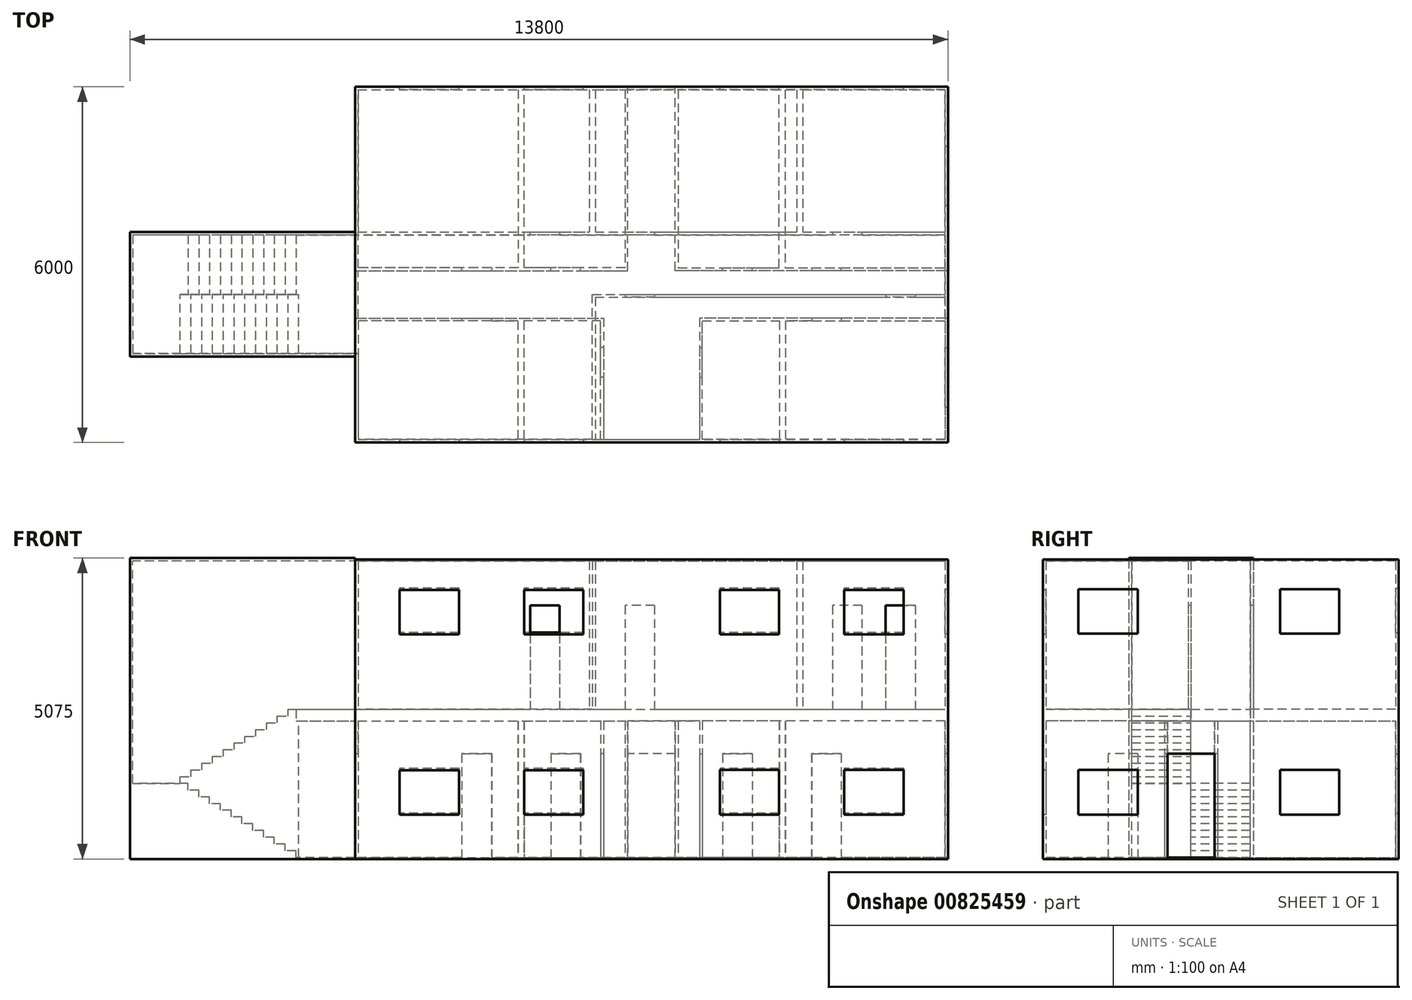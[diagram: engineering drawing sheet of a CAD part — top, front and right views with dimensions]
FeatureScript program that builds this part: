
annotation { "Feature Type Name" : "Feature", "Feature Type Description" : "" }
export const myFeature = defineFeature(function(context is Context, id is Id, definition is map)
    precondition{}
    {
        {
            var Q0;
            Q0=qCreatedBy(makeId("Top.planeOp"),FACE);
            var sketch = newSketch(context, id + "F0", { "sketchPlane" : qUnion([Q0])});
            skLineSegment(sketch, "E0.bottom", {"start": v(0, 0) * mm, "end": v(10000, 0) * mm});
            skLineSegment(sketch, "E0.top", {"start": v(0, 6000) * mm, "end": v(10000, 6000) * mm});
            skLineSegment(sketch, "E0.left", {"start": v(0, 0) * mm, "end": v(0, 6000) * mm});
            skLineSegment(sketch, "E0.right", {"start": v(10000, 0) * mm, "end": v(10000, 6000) * mm});
            skSolve(sketch);
        }
        {
            var Q0;
            Q0=qCreatedBy(makeId("Top.planeOp"),FACE);
            var sketch = newSketch(context, id + "F1", { "sketchPlane" : qUnion([Q0])});
            skLineSegment(sketch, "E1.bottom", {"start": v(0, 0) * mm, "end": v(5000, 0) * mm});
            skLineSegment(sketch, "E1.top", {"start": v(0, 6000) * mm, "end": v(4600, 6000) * mm});
            skLineSegment(sketch, "E1.left", {"start": v(0, 0) * mm, "end": v(0, 2100) * mm});
            skLineSegment(sketch, "E2", {"start": v(0, 2900) * mm, "end": v(1800, 2900) * mm});
            skLineSegment(sketch, "E3", {"start": v(0, 2100) * mm, "end": v(1800, 2100) * mm});
            skLineSegment(sketch, "E4", {"start": v(2800, 2900) * mm, "end": v(2800, 6000) * mm});
            skLineSegment(sketch, "E5", {"start": v(2792.35, 2100) * mm, "end": v(2792.35, 0) * mm});
            skLineSegment(sketch, "E6", {"start": v(2800, 2900) * mm, "end": v(3300, 2900) * mm});
            skLineSegment(sketch, "E7", {"start": v(4600, 2900) * mm, "end": v(4600, 6000) * mm});
            skLineSegment(sketch, "E8", {"start": v(2792.35, 2100) * mm, "end": v(4192.35, 2100) * mm});
            skLineSegment(sketch, "E9", {"start": v(4192.35, 2100) * mm, "end": v(4192.35, 1600) * mm});
            skPoint(sketch, "E10", {"position": v(1800, 2900) * mm});
            skPoint(sketch, "E11", {"position": v(2300, 2900) * mm});
            skPoint(sketch, "E12", {"position": v(1800, 2100) * mm});
            skPoint(sketch, "E13", {"position": v(2300, 2100) * mm});
            skPoint(sketch, "E14", {"position": v(4192.35, 1600) * mm});
            skPoint(sketch, "E15", {"position": v(3300, 2900) * mm});
            skPoint(sketch, "E16", {"position": v(3800, 2900) * mm});
            skPoint(sketch, "E17", {"position": v(4192.35, 1100) * mm});
            skLineSegment(sketch, "E18.trimOffspring", {"start": v(2300, 2900) * mm, "end": v(2800, 2900) * mm});
            skLineSegment(sketch, "E19.trimOffspring", {"start": v(2300, 2100) * mm, "end": v(2792.35, 2100) * mm});
            skLineSegment(sketch, "E20.trimOffspring", {"start": v(3800, 2900) * mm, "end": v(4600, 2900) * mm});
            skLineSegment(sketch, "E21.trimOffspring", {"start": v(4192.35, 1100) * mm, "end": v(4192.35, 0) * mm});
            skLineSegment(sketch, "E22.trimOffspring", {"start": v(0, 2900) * mm, "end": v(0, 6000) * mm});
            skLineSegment(sketch, "E23", {"start": v(1800, 2100) * mm, "end": v(1800, 2050) * mm});
            skLineSegment(sketch, "E24", {"start": v(1800, 2050) * mm, "end": v(50, 2050) * mm});
            skLineSegment(sketch, "E25", {"start": v(50, 2050) * mm, "end": v(50, 50) * mm});
            skLineSegment(sketch, "E26", {"start": v(50, 50) * mm, "end": v(2742.35, 50) * mm});
            skLineSegment(sketch, "E27", {"start": v(2300, 2100) * mm, "end": v(2300, 2050) * mm});
            skLineSegment(sketch, "E28", {"start": v(2300, 2050) * mm, "end": v(2742.35, 2050) * mm});
            skLineSegment(sketch, "E29", {"start": v(2742.35, 2050) * mm, "end": v(2742.35, 50) * mm});
            skLineSegment(sketch, "E30", {"start": v(4192.35, 1600) * mm, "end": v(4142.35, 1600) * mm});
            skLineSegment(sketch, "E31", {"start": v(4142.35, 1600) * mm, "end": v(4142.35, 2050) * mm});
            skLineSegment(sketch, "E32", {"start": v(4142.35, 2050) * mm, "end": v(2842.35, 2050) * mm});
            skLineSegment(sketch, "E33", {"start": v(2842.35, 2050) * mm, "end": v(2842.35, 50) * mm});
            skLineSegment(sketch, "E34", {"start": v(2842.35, 50) * mm, "end": v(4142.35, 50) * mm});
            skLineSegment(sketch, "E35", {"start": v(4192.35, 1100) * mm, "end": v(4142.35, 1100) * mm});
            skLineSegment(sketch, "E36", {"start": v(4142.35, 50) * mm, "end": v(4142.35, 1100) * mm});
            skLineSegment(sketch, "E37", {"start": v(4192.35, 50) * mm, "end": v(5000, 50) * mm});
            skLineSegment(sketch, "E38", {"start": v(5000, 0) * mm, "end": v(5000, 50) * mm});
            skLineSegment(sketch, "E39", {"start": v(1800, 2900) * mm, "end": v(1800, 2950) * mm});
            skLineSegment(sketch, "E40", {"start": v(1800, 2950) * mm, "end": v(50, 2950) * mm});
            skLineSegment(sketch, "E41", {"start": v(50, 2950) * mm, "end": v(50, 5950) * mm});
            skLineSegment(sketch, "E42", {"start": v(50, 5950) * mm, "end": v(2750, 5950) * mm});
            skLineSegment(sketch, "E43", {"start": v(2750, 5950) * mm, "end": v(2750, 2950) * mm});
            skLineSegment(sketch, "E44", {"start": v(2750, 2950) * mm, "end": v(2303.7, 2950) * mm});
            skLineSegment(sketch, "E45", {"start": v(2303.7, 2950) * mm, "end": v(2300, 2900) * mm});
            skLineSegment(sketch, "E46", {"start": v(3300, 2900) * mm, "end": v(3300, 2950) * mm});
            skLineSegment(sketch, "E47", {"start": v(3300, 2950) * mm, "end": v(2850, 2950) * mm});
            skLineSegment(sketch, "E48", {"start": v(2850, 2950) * mm, "end": v(2850, 5950) * mm});
            skLineSegment(sketch, "E49", {"start": v(2850, 5950) * mm, "end": v(4550, 5950) * mm});
            skLineSegment(sketch, "E50", {"start": v(4550, 5950) * mm, "end": v(4550, 2950) * mm});
            skLineSegment(sketch, "E51", {"start": v(4550, 2950) * mm, "end": v(3800.9, 2950) * mm});
            skLineSegment(sketch, "E52", {"start": v(3800, 2900) * mm, "end": v(3800.9, 2950) * mm});
            skSolve(sketch);
        }
        {
            var Q0;
            Q0=qSketchRegion(id+"F0",true);
            extrude(context, id + "F2", {"entities" : qUnion([Q0]), "oppositeDirection" : true, "depth" : 25 * mm, "offsetDistance" : 25 * mm});
        }
        {
            var Q0;
            Q0=qSketchRegion(id+"F1",true);
            extrude(context, id + "F3", {"entities" : qUnion([Q0]), "operationType" : NewBodyOperationType.ADD, "depth" : 2500 * mm, "offsetDistance" : 25 * mm});
        }
        {
            var Q0;
            Q0=qCreatedBy(makeId("Top.planeOp"),FACE);
            cPlane(context, id + "F4", {"entities" : qUnion([Q0]), "cplaneType" : CPlaneType.OFFSET, "offset" : 2500 * mm, "width" : 150 * mm, "height" : 150 * mm});
        }
        {
            var Q0;
            Q0=qCreatedBy(id+"F4.planeOp",FACE);
            var sketch = newSketch(context, id + "F5", { "sketchPlane" : qUnion([Q0])});
            skLineSegment(sketch, "E53.bottom", {"start": v(0, 0) * mm, "end": v(10000, 0) * mm});
            skLineSegment(sketch, "E53.top", {"start": v(0, 6000) * mm, "end": v(10000, 6000) * mm});
            skLineSegment(sketch, "E53.left", {"start": v(0, 0) * mm, "end": v(0, 6000) * mm});
            skLineSegment(sketch, "E53.right", {"start": v(10000, 0) * mm, "end": v(10000, 6000) * mm});
            skSolve(sketch);
        }
        {
            var Q0;
            Q0=qSketchRegion(id+"F5",true);
            extrude(context, id + "F6", {"entities" : qUnion([Q0]), "operationType" : NewBodyOperationType.ADD, "oppositeDirection" : true, "depth" : 200 * mm, "offsetDistance" : 25 * mm});
        }
        {
            var Q0;
            Q0=qCreatedBy(id+"F4.planeOp",FACE);
            var sketch = newSketch(context, id + "F7", { "sketchPlane" : qUnion([Q0])});
            skLineSegment(sketch, "E54.bottom", {"start": v(0, 0) * mm, "end": v(5000, 0) * mm});
            skLineSegment(sketch, "E54.top", {"start": v(0, 6000) * mm, "end": v(4600, 6000) * mm});
            skLineSegment(sketch, "E54.left", {"start": v(0, 0) * mm, "end": v(0, 2100) * mm});
            skLineSegment(sketch, "E55", {"start": v(0, 2900) * mm, "end": v(1800, 2900) * mm});
            skLineSegment(sketch, "E56", {"start": v(0, 2100) * mm, "end": v(1800, 2100) * mm});
            skLineSegment(sketch, "E57", {"start": v(2800, 2900) * mm, "end": v(2800, 6000) * mm});
            skLineSegment(sketch, "E58", {"start": v(2792.35, 2100) * mm, "end": v(2792.35, 0) * mm});
            skLineSegment(sketch, "E59", {"start": v(2800, 2900) * mm, "end": v(3300, 2900) * mm});
            skLineSegment(sketch, "E60", {"start": v(4600, 2900) * mm, "end": v(4600, 6000) * mm});
            skLineSegment(sketch, "E61", {"start": v(2792.35, 2100) * mm, "end": v(4192.35, 2100) * mm});
            skLineSegment(sketch, "E62", {"start": v(4192.35, 2100) * mm, "end": v(4192.35, 1600) * mm});
            skPoint(sketch, "E63", {"position": v(1800, 2900) * mm});
            skPoint(sketch, "E64", {"position": v(2300, 2900) * mm});
            skPoint(sketch, "E65", {"position": v(1800, 2100) * mm});
            skPoint(sketch, "E66", {"position": v(2300, 2100) * mm});
            skPoint(sketch, "E67", {"position": v(4192.35, 1600) * mm});
            skPoint(sketch, "E68", {"position": v(3300, 2900) * mm});
            skPoint(sketch, "E69", {"position": v(3800, 2900) * mm});
            skPoint(sketch, "E70", {"position": v(4192.35, 1100) * mm});
            skLineSegment(sketch, "E71.trimOffspring", {"start": v(2300, 2900) * mm, "end": v(2800, 2900) * mm});
            skLineSegment(sketch, "E72.trimOffspring", {"start": v(2300, 2100) * mm, "end": v(2792.35, 2100) * mm});
            skLineSegment(sketch, "E73.trimOffspring", {"start": v(3800, 2900) * mm, "end": v(4600, 2900) * mm});
            skLineSegment(sketch, "E74.trimOffspring", {"start": v(4192.35, 1100) * mm, "end": v(4192.35, 0) * mm});
            skLineSegment(sketch, "E75.trimOffspring", {"start": v(0, 2900) * mm, "end": v(0, 6000) * mm});
            skLineSegment(sketch, "E76", {"start": v(1800, 2100) * mm, "end": v(1800, 2050) * mm});
            skLineSegment(sketch, "E77", {"start": v(1800, 2050) * mm, "end": v(50, 2050) * mm});
            skLineSegment(sketch, "E78", {"start": v(50, 2050) * mm, "end": v(50, 50) * mm});
            skLineSegment(sketch, "E79", {"start": v(50, 50) * mm, "end": v(2742.35, 50) * mm});
            skLineSegment(sketch, "E80", {"start": v(2300, 2100) * mm, "end": v(2300, 2050) * mm});
            skLineSegment(sketch, "E81", {"start": v(2300, 2050) * mm, "end": v(2742.35, 2050) * mm});
            skLineSegment(sketch, "E82", {"start": v(2742.35, 2050) * mm, "end": v(2742.35, 50) * mm});
            skLineSegment(sketch, "E83", {"start": v(4192.35, 1600) * mm, "end": v(4142.35, 1600) * mm});
            skLineSegment(sketch, "E84", {"start": v(4142.35, 1600) * mm, "end": v(4142.35, 2050) * mm});
            skLineSegment(sketch, "E85", {"start": v(4142.35, 2050) * mm, "end": v(2842.35, 2050) * mm});
            skLineSegment(sketch, "E86", {"start": v(2842.35, 2050) * mm, "end": v(2842.35, 50) * mm});
            skLineSegment(sketch, "E87", {"start": v(2842.35, 50) * mm, "end": v(4142.35, 50) * mm});
            skLineSegment(sketch, "E88", {"start": v(4192.35, 1100) * mm, "end": v(4142.35, 1100) * mm});
            skLineSegment(sketch, "E89", {"start": v(4142.35, 50) * mm, "end": v(4142.35, 1100) * mm});
            skLineSegment(sketch, "E90", {"start": v(4192.35, 50) * mm, "end": v(5000, 50) * mm});
            skLineSegment(sketch, "E91", {"start": v(5000, 0) * mm, "end": v(5000, 50) * mm});
            skLineSegment(sketch, "E92", {"start": v(1800, 2900) * mm, "end": v(1800, 2950) * mm});
            skLineSegment(sketch, "E93", {"start": v(1800, 2950) * mm, "end": v(50, 2950) * mm});
            skLineSegment(sketch, "E94", {"start": v(50, 2950) * mm, "end": v(50, 5950) * mm});
            skLineSegment(sketch, "E95", {"start": v(50, 5950) * mm, "end": v(2750, 5950) * mm});
            skLineSegment(sketch, "E96", {"start": v(2750, 5950) * mm, "end": v(2750, 2950) * mm});
            skLineSegment(sketch, "E97", {"start": v(2750, 2950) * mm, "end": v(2303.7, 2950) * mm});
            skLineSegment(sketch, "E98", {"start": v(2303.7, 2950) * mm, "end": v(2300, 2900) * mm});
            skLineSegment(sketch, "E99", {"start": v(3300, 2900) * mm, "end": v(3300, 2950) * mm});
            skLineSegment(sketch, "E100", {"start": v(3300, 2950) * mm, "end": v(2850, 2950) * mm});
            skLineSegment(sketch, "E101", {"start": v(2850, 2950) * mm, "end": v(2850, 5950) * mm});
            skLineSegment(sketch, "E102", {"start": v(2850, 5950) * mm, "end": v(4550, 5950) * mm});
            skLineSegment(sketch, "E103", {"start": v(4550, 5950) * mm, "end": v(4550, 2950) * mm});
            skLineSegment(sketch, "E104", {"start": v(4550, 2950) * mm, "end": v(3800.9, 2950) * mm});
            skLineSegment(sketch, "E105", {"start": v(3800, 2900) * mm, "end": v(3800.9, 2950) * mm});
            skLineSegment(sketch, "E106", {"start": v(0, 2900) * mm, "end": v(0, 2100) * mm});
            skLineSegment(sketch, "E107", {"start": v(50, 2050) * mm, "end": v(50, 2950) * mm});
            skLineSegment(sketch, "E108", {"start": v(1800, 2050) * mm, "end": v(2300, 2050) * mm});
            skLineSegment(sketch, "E109", {"start": v(2300, 2100) * mm, "end": v(1800, 2100) * mm});
            skLineSegment(sketch, "E110", {"start": v(1800, 2900) * mm, "end": v(2300, 2900) * mm});
            skLineSegment(sketch, "E111", {"start": v(1800, 2950) * mm, "end": v(2303.7, 2950) * mm});
            skLineSegment(sketch, "E112", {"start": v(3300, 2900) * mm, "end": v(3800, 2900) * mm});
            skLineSegment(sketch, "E113", {"start": v(3800.9, 2950) * mm, "end": v(3300, 2950) * mm});
            skLineSegment(sketch, "E114", {"start": v(4192.35, 1600) * mm, "end": v(4192.35, 1100) * mm});
            skLineSegment(sketch, "E115", {"start": v(4142.35, 1100) * mm, "end": v(4142.35, 1600) * mm});
            skLineSegment(sketch, "E116", {"start": v(4600, 6000) * mm, "end": v(5000, 6000) * mm});
            skLineSegment(sketch, "E117", {"start": v(5000, 6000) * mm, "end": v(5000, 5950) * mm});
            skLineSegment(sketch, "E118", {"start": v(5000, 5950) * mm, "end": v(4550, 5950) * mm});
            skSolve(sketch);
        }
        {
            var Q0;
            Q0=qSketchRegion(id+"F7",true);
            extrude(context, id + "F8", {"entities" : qUnion([Q0]), "operationType" : NewBodyOperationType.ADD, "oppositeDirection" : true, "depth" : 750 * mm, "offsetDistance" : 25 * mm});
        }
        {
            var Q0;
            Q0=makeQuery(id+"F2.opExtrude","SWEPT_BODY",BODY,{"disambiguationData":[OSD([sQuery(id+"F0.wireOp",EDGE,"E0.bottom"),sQuery(id+"F0.wireOp",EDGE,"E0.top"),sQuery(id+"F0.wireOp",EDGE,"E0.left"),sQuery(id+"F0.wireOp",EDGE,"E0.right")])]});
            var Q1;
            Q1=makeQuery(id+"F3.opExtrude","SWEPT_FACE",FACE,{"disambiguationData":[OSD([sQuery(id+"F1.wireOp",EDGE,"E38")])]});
            mirror(context, id + "F9", {"operationType" : NewBodyOperationType.ADD, "entities" : qUnion([Q0]), "mirrorPlane" : qUnion([Q1])});
        }
        {
            var Q0;
            Q0=qCreatedBy(makeId("Front.planeOp"),FACE);
            cPlane(context, id + "F10", {"entities" : qUnion([Q0]), "cplaneType" : CPlaneType.OFFSET, "offset" : 2500 * mm, "oppositeDirection" : true, "width" : 150 * mm, "height" : 150 * mm});
        }
        {
            var Q0;
            Q0=qCreatedBy(id+"F10.planeOp",FACE);
            var sketch = newSketch(context, id + "F11", { "sketchPlane" : qUnion([Q0])});
            skLineSegment(sketch, "E119.bottom", {"start": v(-1000, 0) * mm, "end": v(-3000, 0) * mm});
            skLineSegment(sketch, "E119.right", {"start": v(-3000, 0) * mm, "end": v(-3000, 1250) * mm});
            skLineSegment(sketch, "E120", {"start": v(-1000, 0) * mm, "end": v(-3000, 1250) * mm});
            skLineSegment(sketch, "E121.bottom", {"start": v(-1000, 0) * mm, "end": v(-1181.82, 0) * mm});
            skLineSegment(sketch, "E121.top", {"start": v(-1000, 113.64) * mm, "end": v(-1181.82, 113.64) * mm});
            skLineSegment(sketch, "E121.left", {"start": v(-1000, 0) * mm, "end": v(-1000, 113.64) * mm});
            skLineSegment(sketch, "E121.right", {"start": v(-1181.82, 0) * mm, "end": v(-1181.82, 113.64) * mm});
            skLineSegment(sketch, "E122.bottom", {"start": v(-1181.82, 0) * mm, "end": v(-1363.64, 0) * mm});
            skLineSegment(sketch, "E122.top", {"start": v(-1181.82, 227.27) * mm, "end": v(-1363.64, 227.27) * mm});
            skLineSegment(sketch, "E122.left", {"start": v(-1181.82, 0) * mm, "end": v(-1181.82, 227.27) * mm});
            skLineSegment(sketch, "E122.right", {"start": v(-1363.64, 0) * mm, "end": v(-1363.64, 227.27) * mm});
            skLineSegment(sketch, "E123.bottom", {"start": v(-1363.64, 0) * mm, "end": v(-1545.45, 0) * mm});
            skLineSegment(sketch, "E123.top", {"start": v(-1363.64, 340.9) * mm, "end": v(-1545.45, 340.9) * mm});
            skLineSegment(sketch, "E123.left", {"start": v(-1363.64, 0) * mm, "end": v(-1363.64, 340.9) * mm});
            skLineSegment(sketch, "E123.right", {"start": v(-1545.45, 0) * mm, "end": v(-1545.45, 340.9) * mm});
            skLineSegment(sketch, "E124.bottom", {"start": v(-1545.45, 0) * mm, "end": v(-1727.27, 0) * mm});
            skLineSegment(sketch, "E124.top", {"start": v(-1545.45, 454.55) * mm, "end": v(-1727.27, 454.55) * mm});
            skLineSegment(sketch, "E124.left", {"start": v(-1545.45, 0) * mm, "end": v(-1545.45, 454.55) * mm});
            skLineSegment(sketch, "E124.right", {"start": v(-1727.27, 0) * mm, "end": v(-1727.27, 454.55) * mm});
            skLineSegment(sketch, "E125.bottom", {"start": v(-1727.27, 0) * mm, "end": v(-1909.1, 0) * mm});
            skLineSegment(sketch, "E125.top", {"start": v(-1727.27, 568.18) * mm, "end": v(-1909.1, 568.18) * mm});
            skLineSegment(sketch, "E125.left", {"start": v(-1727.27, 0) * mm, "end": v(-1727.27, 568.18) * mm});
            skLineSegment(sketch, "E125.right", {"start": v(-1909.1, 0) * mm, "end": v(-1909.1, 568.18) * mm});
            skLineSegment(sketch, "E126.bottom", {"start": v(-1909.1, 0) * mm, "end": v(-2090.9, 0) * mm});
            skLineSegment(sketch, "E126.top", {"start": v(-1909.1, 681.81) * mm, "end": v(-2090.9, 681.81) * mm});
            skLineSegment(sketch, "E126.left", {"start": v(-1909.1, 0) * mm, "end": v(-1909.1, 681.81) * mm});
            skLineSegment(sketch, "E126.right", {"start": v(-2090.9, 0) * mm, "end": v(-2090.9, 681.81) * mm});
            skLineSegment(sketch, "E127.bottom", {"start": v(-2090.9, 0) * mm, "end": v(-2272.72, 0) * mm});
            skLineSegment(sketch, "E127.top", {"start": v(-2090.9, 795.45) * mm, "end": v(-2272.72, 795.45) * mm});
            skLineSegment(sketch, "E127.left", {"start": v(-2090.9, 0) * mm, "end": v(-2090.9, 795.45) * mm});
            skLineSegment(sketch, "E127.right", {"start": v(-2272.72, 0) * mm, "end": v(-2272.72, 795.45) * mm});
            skLineSegment(sketch, "E128.bottom", {"start": v(-2272.72, 0) * mm, "end": v(-2454.54, 0) * mm});
            skLineSegment(sketch, "E128.top", {"start": v(-2272.72, 909.09) * mm, "end": v(-2454.54, 909.09) * mm});
            skLineSegment(sketch, "E128.left", {"start": v(-2272.72, 0) * mm, "end": v(-2272.72, 909.09) * mm});
            skLineSegment(sketch, "E128.right", {"start": v(-2454.54, 0) * mm, "end": v(-2454.54, 909.09) * mm});
            skLineSegment(sketch, "E129.bottom", {"start": v(-2454.54, 0) * mm, "end": v(-2636.36, 0) * mm});
            skLineSegment(sketch, "E129.top", {"start": v(-2454.54, 1022.72) * mm, "end": v(-2636.36, 1022.72) * mm});
            skLineSegment(sketch, "E129.left", {"start": v(-2454.54, 0) * mm, "end": v(-2454.54, 1022.72) * mm});
            skLineSegment(sketch, "E129.right", {"start": v(-2636.36, 0) * mm, "end": v(-2636.36, 1022.72) * mm});
            skLineSegment(sketch, "E130.bottom", {"start": v(-2636.36, 0) * mm, "end": v(-2818.17, 0) * mm});
            skLineSegment(sketch, "E130.top", {"start": v(-2636.36, 1136.36) * mm, "end": v(-2818.17, 1136.36) * mm});
            skLineSegment(sketch, "E130.left", {"start": v(-2636.36, 0) * mm, "end": v(-2636.36, 1136.36) * mm});
            skLineSegment(sketch, "E130.right", {"start": v(-2818.17, 0) * mm, "end": v(-2818.17, 1136.36) * mm});
            skLineSegment(sketch, "E131.bottom", {"start": v(-3000, 0) * mm, "end": v(-3750, 0) * mm});
            skLineSegment(sketch, "E131.top", {"start": v(-3000, 1250) * mm, "end": v(-3750, 1250) * mm});
            skLineSegment(sketch, "E131.right", {"start": v(-3750, 0) * mm, "end": v(-3750, 1250) * mm});
            skLineSegment(sketch, "E132.bottom", {"start": v(-2818.17, 0) * mm, "end": v(-3000, 0) * mm});
            skLineSegment(sketch, "E132.top", {"start": v(-2818.17, 1250) * mm, "end": v(-3000, 1250) * mm});
            skLineSegment(sketch, "E132.left", {"start": v(-2818.17, 0) * mm, "end": v(-2818.17, 1250) * mm});
            skSolve(sketch);
        }
        {
            var Q0;
            Q0=qSketchRegion(id+"F11",true);
            extrude(context, id + "F12", {"entities" : qUnion([Q0]), "operationType" : NewBodyOperationType.ADD, "oppositeDirection" : true, "depth" : 1000 * mm, "offsetDistance" : 25 * mm});
        }
        {
            var Q0;
            Q0=qCreatedBy(id+"F10.planeOp",FACE);
            var sketch = newSketch(context, id + "F13", { "sketchPlane" : qUnion([Q0])});
            skLineSegment(sketch, "E133.bottom", {"start": v(-3750, 0) * mm, "end": v(-2950, 0) * mm});
            skLineSegment(sketch, "E133.top", {"start": v(-3750, 1250) * mm, "end": v(-2950, 1250) * mm});
            skLineSegment(sketch, "E133.left", {"start": v(-3750, 0) * mm, "end": v(-3750, 1250) * mm});
            skLineSegment(sketch, "E133.right", {"start": v(-2950, 0) * mm, "end": v(-2950, 1250) * mm});
            skLineSegment(sketch, "E134", {"start": v(-2950, 1250) * mm, "end": v(-950, 1250) * mm});
            skLineSegment(sketch, "E135", {"start": v(-2950, 0) * mm, "end": v(-950, 0) * mm});
            skLineSegment(sketch, "E136", {"start": v(-950, 0) * mm, "end": v(-950, 1250) * mm});
            skLineSegment(sketch, "E137", {"start": v(-950, 1250) * mm, "end": v(-950, 2500) * mm});
            skLineSegment(sketch, "E138", {"start": v(-2950, 1250) * mm, "end": v(-950, 2500) * mm});
            skLineSegment(sketch, "E139.bottom", {"start": v(-2950, 1250) * mm, "end": v(-2768.18, 1250) * mm});
            skLineSegment(sketch, "E139.top", {"start": v(-2950, 1363.64) * mm, "end": v(-2768.18, 1363.64) * mm});
            skLineSegment(sketch, "E139.left", {"start": v(-2950, 1250) * mm, "end": v(-2950, 1363.64) * mm});
            skLineSegment(sketch, "E139.right", {"start": v(-2768.18, 1250) * mm, "end": v(-2768.18, 1363.64) * mm});
            skLineSegment(sketch, "E140.bottom", {"start": v(-2768.18, 1250) * mm, "end": v(-2586.36, 1250) * mm});
            skLineSegment(sketch, "E140.top", {"start": v(-2768.18, 1477.27) * mm, "end": v(-2586.36, 1477.27) * mm});
            skLineSegment(sketch, "E140.left", {"start": v(-2768.18, 1250) * mm, "end": v(-2768.18, 1477.27) * mm});
            skLineSegment(sketch, "E140.right", {"start": v(-2586.36, 1250) * mm, "end": v(-2586.36, 1477.27) * mm});
            skLineSegment(sketch, "E141.bottom", {"start": v(-2586.36, 1250) * mm, "end": v(-2404.55, 1250) * mm});
            skLineSegment(sketch, "E141.top", {"start": v(-2586.36, 1590.9) * mm, "end": v(-2404.55, 1590.9) * mm});
            skLineSegment(sketch, "E141.left", {"start": v(-2586.36, 1250) * mm, "end": v(-2586.36, 1590.9) * mm});
            skLineSegment(sketch, "E141.right", {"start": v(-2404.55, 1250) * mm, "end": v(-2404.55, 1590.9) * mm});
            skLineSegment(sketch, "E142.bottom", {"start": v(-2404.55, 1250) * mm, "end": v(-2222.74, 1250) * mm});
            skLineSegment(sketch, "E142.top", {"start": v(-2404.55, 1704.54) * mm, "end": v(-2222.74, 1704.54) * mm});
            skLineSegment(sketch, "E142.left", {"start": v(-2404.55, 1250) * mm, "end": v(-2404.55, 1704.54) * mm});
            skLineSegment(sketch, "E142.right", {"start": v(-2222.74, 1250) * mm, "end": v(-2222.74, 1704.54) * mm});
            skLineSegment(sketch, "E143.bottom", {"start": v(-2222.74, 1250) * mm, "end": v(-2040.92, 1250) * mm});
            skLineSegment(sketch, "E143.top", {"start": v(-2222.74, 1818.18) * mm, "end": v(-2040.92, 1818.18) * mm});
            skLineSegment(sketch, "E143.left", {"start": v(-2222.74, 1250) * mm, "end": v(-2222.74, 1818.18) * mm});
            skLineSegment(sketch, "E143.right", {"start": v(-2040.92, 1250) * mm, "end": v(-2040.92, 1818.18) * mm});
            skLineSegment(sketch, "E144.bottom", {"start": v(-2040.92, 1250) * mm, "end": v(-1859.1, 1250) * mm});
            skLineSegment(sketch, "E144.top", {"start": v(-2040.92, 1931.81) * mm, "end": v(-1859.1, 1931.81) * mm});
            skLineSegment(sketch, "E144.left", {"start": v(-2040.92, 1250) * mm, "end": v(-2040.92, 1931.81) * mm});
            skLineSegment(sketch, "E144.right", {"start": v(-1859.1, 1250) * mm, "end": v(-1859.1, 1931.81) * mm});
            skLineSegment(sketch, "E145.bottom", {"start": v(-1859.1, 1250) * mm, "end": v(-1677.29, 1250) * mm});
            skLineSegment(sketch, "E145.top", {"start": v(-1859.1, 2045.44) * mm, "end": v(-1677.29, 2045.44) * mm});
            skLineSegment(sketch, "E145.left", {"start": v(-1859.1, 1250) * mm, "end": v(-1859.1, 2045.44) * mm});
            skLineSegment(sketch, "E145.right", {"start": v(-1677.29, 1250) * mm, "end": v(-1677.29, 2045.44) * mm});
            skLineSegment(sketch, "E146.bottom", {"start": v(-1677.29, 1250) * mm, "end": v(-1495.47, 1250) * mm});
            skLineSegment(sketch, "E146.top", {"start": v(-1677.29, 2159.08) * mm, "end": v(-1495.47, 2159.08) * mm});
            skLineSegment(sketch, "E146.left", {"start": v(-1677.29, 1250) * mm, "end": v(-1677.29, 2159.08) * mm});
            skLineSegment(sketch, "E146.right", {"start": v(-1495.47, 1250) * mm, "end": v(-1495.47, 2159.08) * mm});
            skLineSegment(sketch, "E147.bottom", {"start": v(-1495.47, 1250) * mm, "end": v(-1313.65, 1250) * mm});
            skLineSegment(sketch, "E147.top", {"start": v(-1495.47, 2272.72) * mm, "end": v(-1313.65, 2272.72) * mm});
            skLineSegment(sketch, "E147.left", {"start": v(-1495.47, 1250) * mm, "end": v(-1495.47, 2272.72) * mm});
            skLineSegment(sketch, "E147.right", {"start": v(-1313.65, 1250) * mm, "end": v(-1313.65, 2272.72) * mm});
            skLineSegment(sketch, "E148.bottom", {"start": v(-1313.65, 1250) * mm, "end": v(-1131.84, 1250) * mm});
            skLineSegment(sketch, "E148.top", {"start": v(-1313.65, 2386.35) * mm, "end": v(-1131.84, 2386.35) * mm});
            skLineSegment(sketch, "E148.left", {"start": v(-1313.65, 1250) * mm, "end": v(-1313.65, 2386.35) * mm});
            skLineSegment(sketch, "E148.right", {"start": v(-1131.84, 1250) * mm, "end": v(-1131.84, 2386.35) * mm});
            skLineSegment(sketch, "E149.bottom", {"start": v(-1131.84, 1250) * mm, "end": v(-950, 1250) * mm});
            skLineSegment(sketch, "E149.top", {"start": v(-1131.84, 2500) * mm, "end": v(-950, 2500) * mm});
            skLineSegment(sketch, "E149.left", {"start": v(-1131.84, 1250) * mm, "end": v(-1131.84, 2500) * mm});
            skSolve(sketch);
        }
        {
            var Q0;
            Q0=qSketchRegion(id+"F13",true);
            extrude(context, id + "F14", {"entities" : qUnion([Q0]), "operationType" : NewBodyOperationType.ADD, "depth" : 1000 * mm, "offsetDistance" : 25 * mm});
        }
        {
            var Q0;
            Q0=makeQuery(id+"F8.boolean.opBoolean","MERGE",FACE,{"derivedFrom":[makeQuery(id+"F6.boolean.opBoolean","MERGE",FACE,{"derivedFrom":[makeQuery(id+"F3.boolean.opBoolean","MERGE",FACE,{"derivedFrom":[makeQuery(id+"F2.opExtrude","SWEPT_FACE",FACE,{"disambiguationData":[OSD([sQuery(id+"F0.wireOp",EDGE,"E0.left")])]}),makeQuery(id+"F3.opExtrude","SWEPT_FACE",FACE,{"disambiguationData":[OSD([sQuery(id+"F1.wireOp",EDGE,"E1.left")])]}),makeQuery(id+"F3.opExtrude","SWEPT_FACE",FACE,{"disambiguationData":[OSD([sQuery(id+"F1.wireOp",EDGE,"E22.trimOffspring")])]})]}),makeQuery(id+"F6.opExtrude","SWEPT_FACE",FACE,{"disambiguationData":[OSD([sQuery(id+"F5.wireOp",EDGE,"E53.left")])]})]}),makeQuery(id+"F8.opExtrude","SWEPT_FACE",FACE,{"disambiguationData":[OSD([sQuery(id+"F7.wireOp",EDGE,"E54.left"),sQuery(id+"F7.wireOp",EDGE,"E75.trimOffspring"),sQuery(id+"F7.wireOp",EDGE,"E106")])]})]});
            var sketch = newSketch(context, id + "F15", { "sketchPlane" : qUnion([Q0])});
            skLineSegment(sketch, "E150.top", {"start": v(-1500, 2500) * mm, "end": v(-3500, 2500) * mm});
            skLineSegment(sketch, "E151", {"start": v(-3500, 2500) * mm, "end": v(-3500, 2300) * mm});
            skLineSegment(sketch, "E152", {"start": v(-1500, 2500) * mm, "end": v(-1500, 2300) * mm});
            skLineSegment(sketch, "E153", {"start": v(-1500, 2300) * mm, "end": v(-3500, 2300) * mm});
            skSolve(sketch);
        }
        {
            var Q0;
            Q0=qSketchRegion(id+"F15",true);
            extrude(context, id + "F16", {"entities" : qUnion([Q0]), "operationType" : NewBodyOperationType.ADD, "depth" : 1000 * mm, "offsetDistance" : 25 * mm});
        }
        {
            var Q0;
            Q0=makeQuery(id+"F14.boolean.opBoolean","MERGE",FACE,{"derivedFrom":[makeQuery(id+"F12.opExtrude","SWEPT_FACE",FACE,{"disambiguationData":[OSD([sQuery(id+"F11.wireOp",EDGE,"E131.right")])]}),makeQuery(id+"F14.opExtrude","SWEPT_FACE",FACE,{"disambiguationData":[OSD([sQuery(id+"F13.wireOp",EDGE,"E133.left")])]})]});
            var sketch = newSketch(context, id + "F17", { "sketchPlane" : qUnion([Q0])});
            skLineSegment(sketch, "E154.bottom", {"start": v(-3500, 0) * mm, "end": v(-1500, 0) * mm});
            skLineSegment(sketch, "E154.top", {"start": v(-3500, 5000) * mm, "end": v(-1500, 5000) * mm});
            skLineSegment(sketch, "E154.left", {"start": v(-3500, 0) * mm, "end": v(-3500, 5000) * mm});
            skLineSegment(sketch, "E154.right", {"start": v(-1500, 0) * mm, "end": v(-1500, 5000) * mm});
            skLineSegment(sketch, "E155.bottom", {"start": v(-3550, 5050) * mm, "end": v(-1450, 5050) * mm});
            skLineSegment(sketch, "E155.top", {"start": v(-3550, -25) * mm, "end": v(-1450, -25) * mm});
            skLineSegment(sketch, "E155.left", {"start": v(-3550, 5050) * mm, "end": v(-3550, -25) * mm});
            skLineSegment(sketch, "E155.right", {"start": v(-1450, 5050) * mm, "end": v(-1450, -25) * mm});
            skSolve(sketch);
        }
        {
            var Q0;
            Q0=qSketchRegion(id+"F17",true);
            extrude(context, id + "F18", {"entities" : qUnion([Q0]), "operationType" : NewBodyOperationType.ADD, "oppositeDirection" : true, "depth" : 3750 * mm, "offsetDistance" : 25 * mm});
        }
        {
            var Q0;
            Q0=makeQuery(id+"F18.boolean.opBoolean","MERGE",FACE,{"derivedFrom":[makeQuery(id+"F14.boolean.opBoolean","MERGE",FACE,{"derivedFrom":[makeQuery(id+"F12.opExtrude","SWEPT_FACE",FACE,{"disambiguationData":[OSD([sQuery(id+"F11.wireOp",EDGE,"E131.right")])]}),makeQuery(id+"F14.opExtrude","SWEPT_FACE",FACE,{"disambiguationData":[OSD([sQuery(id+"F13.wireOp",EDGE,"E133.left")])]})]}),makeQuery(id+"F18.opExtrude","CAP_FACE",FACE,{"disambiguationData":[OSD([sQuery(id+"F17.wireOp",EDGE,"E154.bottom"),sQuery(id+"F17.wireOp",EDGE,"E154.top"),sQuery(id+"F17.wireOp",EDGE,"E154.left"),sQuery(id+"F17.wireOp",EDGE,"E154.right"),sQuery(id+"F17.wireOp",EDGE,"E155.bottom"),sQuery(id+"F17.wireOp",EDGE,"E155.top"),sQuery(id+"F17.wireOp",EDGE,"E155.left"),sQuery(id+"F17.wireOp",EDGE,"E155.right")])],"isStart":true})]});
            var sketch = newSketch(context, id + "F19", { "sketchPlane" : qUnion([Q0])});
            skLineSegment(sketch, "E156.bottom", {"start": v(-3550, -25) * mm, "end": v(-1450, -25) * mm});
            skLineSegment(sketch, "E156.top", {"start": v(-3550, 5050) * mm, "end": v(-1450, 5050) * mm});
            skLineSegment(sketch, "E156.left", {"start": v(-3550, -25) * mm, "end": v(-3550, 5050) * mm});
            skLineSegment(sketch, "E156.right", {"start": v(-1450, -25) * mm, "end": v(-1450, 5050) * mm});
            skSolve(sketch);
        }
        {
            var Q0;
            Q0=qSketchRegion(id+"F19",true);
            extrude(context, id + "F20", {"entities" : qUnion([Q0]), "operationType" : NewBodyOperationType.ADD, "depth" : 50 * mm, "offsetDistance" : 25 * mm});
        }
        {
            var Q0;
            {var subQ0=sQuery(id+"F5.wireOp",EDGE,"E53.top");var subQ1=sQuery(id+"F1.wireOp",EDGE,"E1.top");Q0=makeQuery(id+"F16.boolean.opBoolean","MERGE",FACE,{"derivedFrom":[makeQuery(id+"F12.boolean.opBoolean","MERGE",FACE,{"derivedFrom":[makeQuery(id+"F6.boolean.opBoolean","MERGE",FACE,{"derivedFrom":[makeQuery(id+"F3.opExtrude","CAP_FACE",FACE,{"disambiguationData":[OSD([sQuery(id+"F1.wireOp",EDGE,"E1.bottom"),sQuery(id+"F1.wireOp",EDGE,"E1.left"),sQuery(id+"F1.wireOp",EDGE,"E3"),sQuery(id+"F1.wireOp",EDGE,"E8"),sQuery(id+"F1.wireOp",EDGE,"E9"),sQuery(id+"F1.wireOp",EDGE,"E19.trimOffspring"),sQuery(id+"F1.wireOp",EDGE,"E21.trimOffspring"),sQuery(id+"F1.wireOp",EDGE,"E23"),sQuery(id+"F1.wireOp",EDGE,"E24"),sQuery(id+"F1.wireOp",EDGE,"E25"),sQuery(id+"F1.wireOp",EDGE,"E26"),sQuery(id+"F1.wireOp",EDGE,"E27"),sQuery(id+"F1.wireOp",EDGE,"E28"),sQuery(id+"F1.wireOp",EDGE,"E29"),sQuery(id+"F1.wireOp",EDGE,"E30"),sQuery(id+"F1.wireOp",EDGE,"E31"),sQuery(id+"F1.wireOp",EDGE,"E32"),sQuery(id+"F1.wireOp",EDGE,"E33"),sQuery(id+"F1.wireOp",EDGE,"E34"),sQuery(id+"F1.wireOp",EDGE,"E35"),sQuery(id+"F1.wireOp",EDGE,"E36"),sQuery(id+"F1.wireOp",EDGE,"E37"),sQuery(id+"F1.wireOp",EDGE,"E38")])],"isStart":false}),makeQuery(id+"F3.opExtrude","CAP_FACE",FACE,{"disambiguationData":[OSD([subQ1,sQuery(id+"F1.wireOp",EDGE,"E2"),sQuery(id+"F1.wireOp",EDGE,"E6"),sQuery(id+"F1.wireOp",EDGE,"E7"),sQuery(id+"F1.wireOp",EDGE,"E18.trimOffspring"),sQuery(id+"F1.wireOp",EDGE,"E20.trimOffspring"),sQuery(id+"F1.wireOp",EDGE,"E22.trimOffspring"),sQuery(id+"F1.wireOp",EDGE,"E39"),sQuery(id+"F1.wireOp",EDGE,"E40"),sQuery(id+"F1.wireOp",EDGE,"E41"),sQuery(id+"F1.wireOp",EDGE,"E42"),sQuery(id+"F1.wireOp",EDGE,"E43"),sQuery(id+"F1.wireOp",EDGE,"E44"),sQuery(id+"F1.wireOp",EDGE,"E45"),sQuery(id+"F1.wireOp",EDGE,"E46"),sQuery(id+"F1.wireOp",EDGE,"E47"),sQuery(id+"F1.wireOp",EDGE,"E48"),sQuery(id+"F1.wireOp",EDGE,"E49"),sQuery(id+"F1.wireOp",EDGE,"E50"),sQuery(id+"F1.wireOp",EDGE,"E51"),sQuery(id+"F1.wireOp",EDGE,"E52")])],"isStart":false}),makeQuery(id+"F6.opExtrude","CAP_FACE",FACE,{"disambiguationData":[OSD([sQuery(id+"F5.wireOp",EDGE,"E53.bottom"),subQ0,sQuery(id+"F5.wireOp",EDGE,"E53.left"),sQuery(id+"F5.wireOp",EDGE,"E53.right")])],"isStart":true})]}),makeQuery(id+"F12.opExtrude","SWEPT_FACE",FACE,{"disambiguationData":[OSD([subQ1,subQ0])]})]}),makeQuery(id+"F14.opExtrude","SWEPT_FACE",FACE,{"disambiguationData":[OSD([sQuery(id+"F13.wireOp",EDGE,"E149.top")])]}),makeQuery(id+"F16.opExtrude","SWEPT_FACE",FACE,{"disambiguationData":[OSD([sQuery(id+"F15.wireOp",EDGE,"E150.top")])]})]});}
            var sketch = newSketch(context, id + "F21", { "sketchPlane" : qUnion([Q0])});
            skLineSegment(sketch, "E157.bottom", {"start": v(0, 6000) * mm, "end": v(10000, 6000) * mm});
            skLineSegment(sketch, "E157.top", {"start": v(0, 0) * mm, "end": v(10000, 0) * mm});
            skLineSegment(sketch, "E157.right", {"start": v(10000, 6000) * mm, "end": v(10000, 0) * mm});
            skPoint(sketch, "E158", {"position": v(0, 3550) * mm});
            skPoint(sketch, "E159", {"position": v(0, 1450) * mm});
            skLineSegment(sketch, "E160.trimOffspring", {"start": v(0, 1450) * mm, "end": v(0, 0) * mm});
            skLineSegment(sketch, "E161", {"start": v(4000, 3500) * mm, "end": v(4000, 6000) * mm});
            skLineSegment(sketch, "E162", {"start": v(4000, 0) * mm, "end": v(4000, 2500) * mm});
            skLineSegment(sketch, "E163", {"start": v(4000, 2500) * mm, "end": v(4550, 2500) * mm});
            skLineSegment(sketch, "E164", {"start": v(4000, 3500) * mm, "end": v(4550, 3500) * mm});
            skLineSegment(sketch, "E165", {"start": v(7500, 3500) * mm, "end": v(7500, 6000) * mm});
            skLineSegment(sketch, "E166", {"start": v(7500, 3500) * mm, "end": v(8050, 3500) * mm});
            skLineSegment(sketch, "E167.bottom", {"start": v(50, 5950) * mm, "end": v(3950, 5950) * mm});
            skLineSegment(sketch, "E167.top", {"start": v(50, 3550) * mm, "end": v(2950, 3550) * mm});
            skLineSegment(sketch, "E167.left", {"start": v(50, 5950) * mm, "end": v(50, 3550) * mm});
            skLineSegment(sketch, "E167.right", {"start": v(3950, 5950) * mm, "end": v(3950, 3550) * mm});
            skLineSegment(sketch, "E168.bottom", {"start": v(4050, 5950) * mm, "end": v(7450, 5950) * mm});
            skLineSegment(sketch, "E168.top", {"start": v(4050, 3550) * mm, "end": v(4550, 3550) * mm});
            skLineSegment(sketch, "E168.left", {"start": v(4050, 5950) * mm, "end": v(4050, 3550) * mm});
            skLineSegment(sketch, "E168.right", {"start": v(7450, 5950) * mm, "end": v(7450, 3550) * mm});
            skLineSegment(sketch, "E169.bottom", {"start": v(7550, 5950) * mm, "end": v(9950, 5950) * mm});
            skLineSegment(sketch, "E169.top", {"start": v(7550, 3550) * mm, "end": v(8050, 3550) * mm});
            skLineSegment(sketch, "E169.left", {"start": v(7550, 5950) * mm, "end": v(7550, 3550) * mm});
            skLineSegment(sketch, "E169.right", {"start": v(9950, 5950) * mm, "end": v(9950, 3550) * mm});
            skLineSegment(sketch, "E170", {"start": v(9950, 3500) * mm, "end": v(9950, 2500) * mm});
            skLineSegment(sketch, "E171.bottom", {"start": v(4050, 2450) * mm, "end": v(4550, 2450) * mm});
            skLineSegment(sketch, "E171.top", {"start": v(4050, 50) * mm, "end": v(9950, 50) * mm});
            skLineSegment(sketch, "E171.left", {"start": v(4050, 2450) * mm, "end": v(4050, 50) * mm});
            skLineSegment(sketch, "E171.right", {"start": v(9950, 2450) * mm, "end": v(9950, 50) * mm});
            skLineSegment(sketch, "E172", {"start": v(0, 1450) * mm, "end": v(0, 1500) * mm});
            skLineSegment(sketch, "E173", {"start": v(0, 1500) * mm, "end": v(50, 1500) * mm});
            skLineSegment(sketch, "E174", {"start": v(50, 1500) * mm, "end": v(50, 0) * mm});
            skLineSegment(sketch, "E175", {"start": v(4000, 50) * mm, "end": v(50, 50) * mm});
            skPoint(sketch, "E176", {"position": v(3450, 3550) * mm});
            skPoint(sketch, "E177", {"position": v(2950, 3550) * mm});
            skPoint(sketch, "E178", {"position": v(3450, 3500) * mm});
            skLineSegment(sketch, "E179", {"start": v(3450, 3550) * mm, "end": v(3450, 3500) * mm});
            skLineSegment(sketch, "E180.trimOffspring", {"start": v(3450, 3550) * mm, "end": v(3950, 3550) * mm});
            skLineSegment(sketch, "E181.trimOffspring", {"start": v(3450, 3500) * mm, "end": v(4000, 3500) * mm});
            skPoint(sketch, "E182", {"position": v(4550, 3550) * mm});
            skPoint(sketch, "E183", {"position": v(5050, 3550) * mm});
            skPoint(sketch, "E184", {"position": v(4550, 3500) * mm});
            skPoint(sketch, "E185", {"position": v(5050, 3500) * mm});
            skLineSegment(sketch, "E186", {"start": v(4550, 3550) * mm, "end": v(4550, 3500) * mm});
            skLineSegment(sketch, "E187", {"start": v(5050, 3550) * mm, "end": v(5050, 3500) * mm});
            skLineSegment(sketch, "E188.trimOffspring", {"start": v(5050, 3550) * mm, "end": v(7450, 3550) * mm});
            skLineSegment(sketch, "E189.trimOffspring", {"start": v(5050, 3500) * mm, "end": v(7500, 3500) * mm});
            skPoint(sketch, "E190", {"position": v(8050, 3550) * mm});
            skPoint(sketch, "E191", {"position": v(4550, 2500) * mm});
            skPoint(sketch, "E192", {"position": v(4550, 2450) * mm});
            skPoint(sketch, "E193", {"position": v(5050, 2500) * mm});
            skPoint(sketch, "E194", {"position": v(5050, 2450) * mm});
            skPoint(sketch, "E195", {"position": v(8550, 3550) * mm});
            skPoint(sketch, "E196", {"position": v(8050, 3500) * mm});
            skPoint(sketch, "E197", {"position": v(8550, 3500) * mm});
            skPoint(sketch, "E198", {"position": v(9450, 2500) * mm});
            skPoint(sketch, "E199", {"position": v(9450, 2450) * mm});
            skPoint(sketch, "E200", {"position": v(8950, 2500) * mm});
            skPoint(sketch, "E201", {"position": v(8950, 2450) * mm});
            skLineSegment(sketch, "E202", {"start": v(8950, 2500) * mm, "end": v(8950, 2450) * mm});
            skLineSegment(sketch, "E203", {"start": v(9450, 2500) * mm, "end": v(9450, 2450) * mm});
            skLineSegment(sketch, "E204", {"start": v(8550, 3550) * mm, "end": v(8550, 3500) * mm});
            skLineSegment(sketch, "E205", {"start": v(8050, 3550) * mm, "end": v(8050, 3500) * mm});
            skLineSegment(sketch, "E206", {"start": v(4550, 2500) * mm, "end": v(4550, 2450) * mm});
            skLineSegment(sketch, "E207", {"start": v(5050, 2500) * mm, "end": v(5050, 2450) * mm});
            skLineSegment(sketch, "E208.trimOffspring", {"start": v(5050, 2500) * mm, "end": v(8950, 2500) * mm});
            skLineSegment(sketch, "E209.trimOffspring", {"start": v(5050, 2450) * mm, "end": v(8950, 2450) * mm});
            skLineSegment(sketch, "E210.trimOffspring", {"start": v(8550, 3550) * mm, "end": v(9950, 3550) * mm});
            skLineSegment(sketch, "E211.trimOffspring", {"start": v(8550, 3500) * mm, "end": v(10000, 3500) * mm});
            skLineSegment(sketch, "E212.trimOffspring", {"start": v(9450, 2500) * mm, "end": v(10000, 2500) * mm});
            skLineSegment(sketch, "E213.trimOffspring", {"start": v(9450, 2450) * mm, "end": v(9950, 2450) * mm});
            skLineSegment(sketch, "E214", {"start": v(0, 6000) * mm, "end": v(0, 3550) * mm});
            skLineSegment(sketch, "E215", {"start": v(0, 3500) * mm, "end": v(0, 3550) * mm});
            skLineSegment(sketch, "E216", {"start": v(0, 3500) * mm, "end": v(2950, 3500) * mm});
            skLineSegment(sketch, "E217", {"start": v(2950, 3500) * mm, "end": v(2950, 3550) * mm});
            skSolve(sketch);
        }
        {
            var Q0;
            Q0=qSketchRegion(id+"F21",true);
            extrude(context, id + "F22", {"entities" : qUnion([Q0]), "operationType" : NewBodyOperationType.ADD, "depth" : 2500 * mm, "offsetDistance" : 25 * mm});
        }
        {
            var Q0;
            Q0=makeQuery(id+"F22.opExtrude","CAP_FACE",FACE,{"disambiguationData":[OSD([sQuery(id+"F21.wireOp",EDGE,"E157.bottom"),sQuery(id+"F21.wireOp",EDGE,"E157.top"),sQuery(id+"F21.wireOp",EDGE,"E157.right"),sQuery(id+"F21.wireOp",EDGE,"E160.trimOffspring"),sQuery(id+"F21.wireOp",EDGE,"E162"),sQuery(id+"F21.wireOp",EDGE,"E163"),sQuery(id+"F21.wireOp",EDGE,"E164"),sQuery(id+"F21.wireOp",EDGE,"E166"),sQuery(id+"F21.wireOp",EDGE,"E167.bottom"),sQuery(id+"F21.wireOp",EDGE,"E167.top"),sQuery(id+"F21.wireOp",EDGE,"E167.left"),sQuery(id+"F21.wireOp",EDGE,"E167.right"),sQuery(id+"F21.wireOp",EDGE,"E168.bottom"),sQuery(id+"F21.wireOp",EDGE,"E168.top"),sQuery(id+"F21.wireOp",EDGE,"E168.left"),sQuery(id+"F21.wireOp",EDGE,"E168.right"),sQuery(id+"F21.wireOp",EDGE,"E169.bottom"),sQuery(id+"F21.wireOp",EDGE,"E169.top"),sQuery(id+"F21.wireOp",EDGE,"E169.left"),sQuery(id+"F21.wireOp",EDGE,"E169.right"),sQuery(id+"F21.wireOp",EDGE,"E170"),sQuery(id+"F21.wireOp",EDGE,"E171.bottom"),sQuery(id+"F21.wireOp",EDGE,"E171.top"),sQuery(id+"F21.wireOp",EDGE,"E171.left"),sQuery(id+"F21.wireOp",EDGE,"E171.right"),sQuery(id+"F21.wireOp",EDGE,"E172"),sQuery(id+"F21.wireOp",EDGE,"E173"),sQuery(id+"F21.wireOp",EDGE,"E174"),sQuery(id+"F21.wireOp",EDGE,"E175"),sQuery(id+"F21.wireOp",EDGE,"E179"),sQuery(id+"F21.wireOp",EDGE,"E180.trimOffspring"),sQuery(id+"F21.wireOp",EDGE,"E181.trimOffspring"),sQuery(id+"F21.wireOp",EDGE,"E186"),sQuery(id+"F21.wireOp",EDGE,"E187"),sQuery(id+"F21.wireOp",EDGE,"E188.trimOffspring"),sQuery(id+"F21.wireOp",EDGE,"E189.trimOffspring"),sQuery(id+"F21.wireOp",EDGE,"E203"),sQuery(id+"F21.wireOp",EDGE,"E204"),sQuery(id+"F21.wireOp",EDGE,"E205"),sQuery(id+"F21.wireOp",EDGE,"E206"),sQuery(id+"F21.wireOp",EDGE,"E210.trimOffspring"),sQuery(id+"F21.wireOp",EDGE,"E211.trimOffspring"),sQuery(id+"F21.wireOp",EDGE,"E212.trimOffspring"),sQuery(id+"F21.wireOp",EDGE,"E213.trimOffspring"),sQuery(id+"F21.wireOp",EDGE,"E214"),sQuery(id+"F21.wireOp",EDGE,"E215"),sQuery(id+"F21.wireOp",EDGE,"E216"),sQuery(id+"F21.wireOp",EDGE,"E217")])],"isStart":false});
            var sketch = newSketch(context, id + "F23", { "sketchPlane" : qUnion([Q0])});
            skLineSegment(sketch, "E218.bottom", {"start": v(0, 6000) * mm, "end": v(10000, 6000) * mm});
            skLineSegment(sketch, "E218.top", {"start": v(0, 0) * mm, "end": v(10000, 0) * mm});
            skLineSegment(sketch, "E218.right", {"start": v(10000, 6000) * mm, "end": v(10000, 0) * mm});
            skPoint(sketch, "E219", {"position": v(0, 3550) * mm});
            skPoint(sketch, "E220", {"position": v(0, 1450) * mm});
            skLineSegment(sketch, "E221.trimOffspring", {"start": v(0, 1450) * mm, "end": v(0, 0) * mm});
            skLineSegment(sketch, "E222", {"start": v(4000, 3500) * mm, "end": v(4000, 6000) * mm});
            skLineSegment(sketch, "E223", {"start": v(4000, 0) * mm, "end": v(4000, 2500) * mm});
            skLineSegment(sketch, "E224", {"start": v(4000, 2500) * mm, "end": v(4550, 2500) * mm});
            skLineSegment(sketch, "E225", {"start": v(4000, 3500) * mm, "end": v(4550, 3500) * mm});
            skLineSegment(sketch, "E226", {"start": v(7500, 3500) * mm, "end": v(7500, 6000) * mm});
            skLineSegment(sketch, "E227", {"start": v(7500, 3500) * mm, "end": v(8050, 3500) * mm});
            skLineSegment(sketch, "E228.bottom", {"start": v(50, 5950) * mm, "end": v(3950, 5950) * mm});
            skLineSegment(sketch, "E228.top", {"start": v(50, 3550) * mm, "end": v(2950, 3550) * mm});
            skLineSegment(sketch, "E228.left", {"start": v(50, 5950) * mm, "end": v(50, 3550) * mm});
            skLineSegment(sketch, "E228.right", {"start": v(3950, 5950) * mm, "end": v(3950, 3550) * mm});
            skLineSegment(sketch, "E229.bottom", {"start": v(4050, 5950) * mm, "end": v(7450, 5950) * mm});
            skLineSegment(sketch, "E229.top", {"start": v(4050, 3550) * mm, "end": v(4550, 3550) * mm});
            skLineSegment(sketch, "E229.left", {"start": v(4050, 5950) * mm, "end": v(4050, 3550) * mm});
            skLineSegment(sketch, "E229.right", {"start": v(7450, 5950) * mm, "end": v(7450, 3550) * mm});
            skLineSegment(sketch, "E230.bottom", {"start": v(7550, 5950) * mm, "end": v(9950, 5950) * mm});
            skLineSegment(sketch, "E230.top", {"start": v(7550, 3550) * mm, "end": v(8050, 3550) * mm});
            skLineSegment(sketch, "E230.left", {"start": v(7550, 5950) * mm, "end": v(7550, 3550) * mm});
            skLineSegment(sketch, "E230.right", {"start": v(9950, 5950) * mm, "end": v(9950, 3550) * mm});
            skLineSegment(sketch, "E231", {"start": v(9950, 3500) * mm, "end": v(9950, 2500) * mm});
            skLineSegment(sketch, "E232.bottom", {"start": v(4050, 2450) * mm, "end": v(4550, 2450) * mm});
            skLineSegment(sketch, "E232.top", {"start": v(4050, 50) * mm, "end": v(9950, 50) * mm});
            skLineSegment(sketch, "E232.left", {"start": v(4050, 2450) * mm, "end": v(4050, 50) * mm});
            skLineSegment(sketch, "E232.right", {"start": v(9950, 2450) * mm, "end": v(9950, 50) * mm});
            skLineSegment(sketch, "E233", {"start": v(0, 1450) * mm, "end": v(0, 1500) * mm});
            skLineSegment(sketch, "E234", {"start": v(0, 1500) * mm, "end": v(50, 1500) * mm});
            skLineSegment(sketch, "E235", {"start": v(50, 1500) * mm, "end": v(50, 0) * mm});
            skLineSegment(sketch, "E236", {"start": v(4000, 50) * mm, "end": v(50, 50) * mm});
            skPoint(sketch, "E237", {"position": v(3450, 3550) * mm});
            skPoint(sketch, "E238", {"position": v(2950, 3550) * mm});
            skPoint(sketch, "E239", {"position": v(3450, 3500) * mm});
            skLineSegment(sketch, "E240", {"start": v(3450, 3550) * mm, "end": v(3450, 3500) * mm});
            skLineSegment(sketch, "E241.trimOffspring", {"start": v(3450, 3550) * mm, "end": v(3950, 3550) * mm});
            skLineSegment(sketch, "E242.trimOffspring", {"start": v(3450, 3500) * mm, "end": v(4000, 3500) * mm});
            skPoint(sketch, "E243", {"position": v(4550, 3550) * mm});
            skPoint(sketch, "E244", {"position": v(5050, 3550) * mm});
            skPoint(sketch, "E245", {"position": v(4550, 3500) * mm});
            skPoint(sketch, "E246", {"position": v(5050, 3500) * mm});
            skLineSegment(sketch, "E247", {"start": v(4550, 3550) * mm, "end": v(4550, 3500) * mm});
            skLineSegment(sketch, "E248", {"start": v(5050, 3550) * mm, "end": v(5050, 3500) * mm});
            skLineSegment(sketch, "E249.trimOffspring", {"start": v(5050, 3550) * mm, "end": v(7450, 3550) * mm});
            skLineSegment(sketch, "E250.trimOffspring", {"start": v(5050, 3500) * mm, "end": v(7500, 3500) * mm});
            skPoint(sketch, "E251", {"position": v(8050, 3550) * mm});
            skPoint(sketch, "E252", {"position": v(4550, 2500) * mm});
            skPoint(sketch, "E253", {"position": v(4550, 2450) * mm});
            skPoint(sketch, "E254", {"position": v(5050, 2500) * mm});
            skPoint(sketch, "E255", {"position": v(5050, 2450) * mm});
            skPoint(sketch, "E256", {"position": v(8550, 3550) * mm});
            skPoint(sketch, "E257", {"position": v(8050, 3500) * mm});
            skPoint(sketch, "E258", {"position": v(8550, 3500) * mm});
            skPoint(sketch, "E259", {"position": v(9450, 2500) * mm});
            skPoint(sketch, "E260", {"position": v(9450, 2450) * mm});
            skPoint(sketch, "E261", {"position": v(8950, 2500) * mm});
            skPoint(sketch, "E262", {"position": v(8950, 2450) * mm});
            skLineSegment(sketch, "E263", {"start": v(8950, 2500) * mm, "end": v(8950, 2450) * mm});
            skLineSegment(sketch, "E264", {"start": v(9450, 2500) * mm, "end": v(9450, 2450) * mm});
            skLineSegment(sketch, "E265", {"start": v(8550, 3550) * mm, "end": v(8550, 3500) * mm});
            skLineSegment(sketch, "E266", {"start": v(8050, 3550) * mm, "end": v(8050, 3500) * mm});
            skLineSegment(sketch, "E267", {"start": v(4550, 2500) * mm, "end": v(4550, 2450) * mm});
            skLineSegment(sketch, "E268", {"start": v(5050, 2500) * mm, "end": v(5050, 2450) * mm});
            skLineSegment(sketch, "E269.trimOffspring", {"start": v(5050, 2500) * mm, "end": v(8950, 2500) * mm});
            skLineSegment(sketch, "E270.trimOffspring", {"start": v(5050, 2450) * mm, "end": v(8950, 2450) * mm});
            skLineSegment(sketch, "E271.trimOffspring", {"start": v(8550, 3550) * mm, "end": v(9950, 3550) * mm});
            skLineSegment(sketch, "E272.trimOffspring", {"start": v(8550, 3500) * mm, "end": v(10000, 3500) * mm});
            skLineSegment(sketch, "E273.trimOffspring", {"start": v(9450, 2500) * mm, "end": v(10000, 2500) * mm});
            skLineSegment(sketch, "E274.trimOffspring", {"start": v(9450, 2450) * mm, "end": v(9950, 2450) * mm});
            skLineSegment(sketch, "E275", {"start": v(0, 6000) * mm, "end": v(0, 3550) * mm});
            skLineSegment(sketch, "E276", {"start": v(0, 3500) * mm, "end": v(0, 3550) * mm});
            skLineSegment(sketch, "E277", {"start": v(0, 3500) * mm, "end": v(2950, 3500) * mm});
            skLineSegment(sketch, "E278", {"start": v(2950, 3500) * mm, "end": v(2950, 3550) * mm});
            skLineSegment(sketch, "E279", {"start": v(2950, 3550) * mm, "end": v(3450, 3550) * mm});
            skLineSegment(sketch, "E280", {"start": v(3450, 3500) * mm, "end": v(2950, 3500) * mm});
            skLineSegment(sketch, "E281", {"start": v(4550, 3550) * mm, "end": v(5050, 3550) * mm});
            skLineSegment(sketch, "E282", {"start": v(5050, 3500) * mm, "end": v(4550, 3500) * mm});
            skLineSegment(sketch, "E283", {"start": v(4550, 2500) * mm, "end": v(5050, 2500) * mm});
            skLineSegment(sketch, "E284", {"start": v(4550, 2450) * mm, "end": v(5050, 2450) * mm});
            skLineSegment(sketch, "E285", {"start": v(8050, 3550) * mm, "end": v(8550, 3550) * mm});
            skLineSegment(sketch, "E286", {"start": v(8550, 3500) * mm, "end": v(8050, 3500) * mm});
            skLineSegment(sketch, "E287", {"start": v(8950, 2500) * mm, "end": v(9450, 2500) * mm});
            skLineSegment(sketch, "E288", {"start": v(9450, 2450) * mm, "end": v(8950, 2450) * mm});
            skSolve(sketch);
        }
        {
            var Q0;
            Q0=qSketchRegion(id+"F23",true);
            extrude(context, id + "F24", {"entities" : qUnion([Q0]), "operationType" : NewBodyOperationType.ADD, "oppositeDirection" : true, "depth" : 750 * mm, "offsetDistance" : 25 * mm});
        }
        {
            var Q0;
            Q0=makeQuery(id+"F24.boolean.opBoolean","MERGE",FACE,{"derivedFrom":[makeQuery(id+"F22.opExtrude","CAP_FACE",FACE,{"disambiguationData":[OSD([sQuery(id+"F21.wireOp",EDGE,"E157.bottom"),sQuery(id+"F21.wireOp",EDGE,"E157.top"),sQuery(id+"F21.wireOp",EDGE,"E157.right"),sQuery(id+"F21.wireOp",EDGE,"E160.trimOffspring"),sQuery(id+"F21.wireOp",EDGE,"E162"),sQuery(id+"F21.wireOp",EDGE,"E163"),sQuery(id+"F21.wireOp",EDGE,"E164"),sQuery(id+"F21.wireOp",EDGE,"E166"),sQuery(id+"F21.wireOp",EDGE,"E167.bottom"),sQuery(id+"F21.wireOp",EDGE,"E167.top"),sQuery(id+"F21.wireOp",EDGE,"E167.left"),sQuery(id+"F21.wireOp",EDGE,"E167.right"),sQuery(id+"F21.wireOp",EDGE,"E168.bottom"),sQuery(id+"F21.wireOp",EDGE,"E168.top"),sQuery(id+"F21.wireOp",EDGE,"E168.left"),sQuery(id+"F21.wireOp",EDGE,"E168.right"),sQuery(id+"F21.wireOp",EDGE,"E169.bottom"),sQuery(id+"F21.wireOp",EDGE,"E169.top"),sQuery(id+"F21.wireOp",EDGE,"E169.left"),sQuery(id+"F21.wireOp",EDGE,"E169.right"),sQuery(id+"F21.wireOp",EDGE,"E170"),sQuery(id+"F21.wireOp",EDGE,"E171.bottom"),sQuery(id+"F21.wireOp",EDGE,"E171.top"),sQuery(id+"F21.wireOp",EDGE,"E171.left"),sQuery(id+"F21.wireOp",EDGE,"E171.right"),sQuery(id+"F21.wireOp",EDGE,"E172"),sQuery(id+"F21.wireOp",EDGE,"E173"),sQuery(id+"F21.wireOp",EDGE,"E174"),sQuery(id+"F21.wireOp",EDGE,"E175"),sQuery(id+"F21.wireOp",EDGE,"E179"),sQuery(id+"F21.wireOp",EDGE,"E180.trimOffspring"),sQuery(id+"F21.wireOp",EDGE,"E181.trimOffspring"),sQuery(id+"F21.wireOp",EDGE,"E186"),sQuery(id+"F21.wireOp",EDGE,"E187"),sQuery(id+"F21.wireOp",EDGE,"E188.trimOffspring"),sQuery(id+"F21.wireOp",EDGE,"E189.trimOffspring"),sQuery(id+"F21.wireOp",EDGE,"E203"),sQuery(id+"F21.wireOp",EDGE,"E204"),sQuery(id+"F21.wireOp",EDGE,"E205"),sQuery(id+"F21.wireOp",EDGE,"E206"),sQuery(id+"F21.wireOp",EDGE,"E210.trimOffspring"),sQuery(id+"F21.wireOp",EDGE,"E211.trimOffspring"),sQuery(id+"F21.wireOp",EDGE,"E212.trimOffspring"),sQuery(id+"F21.wireOp",EDGE,"E213.trimOffspring"),sQuery(id+"F21.wireOp",EDGE,"E214"),sQuery(id+"F21.wireOp",EDGE,"E215"),sQuery(id+"F21.wireOp",EDGE,"E216"),sQuery(id+"F21.wireOp",EDGE,"E217")])],"isStart":false}),makeQuery(id+"F22.opExtrude","CAP_FACE",FACE,{"disambiguationData":[OSD([sQuery(id+"F21.wireOp",EDGE,"E202"),sQuery(id+"F21.wireOp",EDGE,"E207"),sQuery(id+"F21.wireOp",EDGE,"E208.trimOffspring"),sQuery(id+"F21.wireOp",EDGE,"E209.trimOffspring")])],"isStart":false}),makeQuery(id+"F24.opExtrude","CAP_FACE",FACE,{"disambiguationData":[OSD([sQuery(id+"F23.wireOp",EDGE,"E218.bottom"),sQuery(id+"F23.wireOp",EDGE,"E218.top"),sQuery(id+"F23.wireOp",EDGE,"E218.right"),sQuery(id+"F23.wireOp",EDGE,"E221.trimOffspring"),sQuery(id+"F23.wireOp",EDGE,"E223"),sQuery(id+"F23.wireOp",EDGE,"E224"),sQuery(id+"F23.wireOp",EDGE,"E225"),sQuery(id+"F23.wireOp",EDGE,"E227"),sQuery(id+"F23.wireOp",EDGE,"E228.bottom"),sQuery(id+"F23.wireOp",EDGE,"E228.top"),sQuery(id+"F23.wireOp",EDGE,"E228.left"),sQuery(id+"F23.wireOp",EDGE,"E228.right"),sQuery(id+"F23.wireOp",EDGE,"E229.bottom"),sQuery(id+"F23.wireOp",EDGE,"E229.top"),sQuery(id+"F23.wireOp",EDGE,"E229.left"),sQuery(id+"F23.wireOp",EDGE,"E229.right"),sQuery(id+"F23.wireOp",EDGE,"E230.bottom"),sQuery(id+"F23.wireOp",EDGE,"E230.top"),sQuery(id+"F23.wireOp",EDGE,"E230.left"),sQuery(id+"F23.wireOp",EDGE,"E230.right"),sQuery(id+"F23.wireOp",EDGE,"E231"),sQuery(id+"F23.wireOp",EDGE,"E232.bottom"),sQuery(id+"F23.wireOp",EDGE,"E232.top"),sQuery(id+"F23.wireOp",EDGE,"E232.left"),sQuery(id+"F23.wireOp",EDGE,"E232.right"),sQuery(id+"F23.wireOp",EDGE,"E233"),sQuery(id+"F23.wireOp",EDGE,"E234"),sQuery(id+"F23.wireOp",EDGE,"E235"),sQuery(id+"F23.wireOp",EDGE,"E236"),sQuery(id+"F23.wireOp",EDGE,"E241.trimOffspring"),sQuery(id+"F23.wireOp",EDGE,"E242.trimOffspring"),sQuery(id+"F23.wireOp",EDGE,"E249.trimOffspring"),sQuery(id+"F23.wireOp",EDGE,"E250.trimOffspring"),sQuery(id+"F23.wireOp",EDGE,"E269.trimOffspring"),sQuery(id+"F23.wireOp",EDGE,"E270.trimOffspring"),sQuery(id+"F23.wireOp",EDGE,"E271.trimOffspring"),sQuery(id+"F23.wireOp",EDGE,"E272.trimOffspring"),sQuery(id+"F23.wireOp",EDGE,"E273.trimOffspring"),sQuery(id+"F23.wireOp",EDGE,"E274.trimOffspring"),sQuery(id+"F23.wireOp",EDGE,"E275"),sQuery(id+"F23.wireOp",EDGE,"E276"),sQuery(id+"F23.wireOp",EDGE,"E277"),sQuery(id+"F23.wireOp",EDGE,"E279"),sQuery(id+"F23.wireOp",EDGE,"E280"),sQuery(id+"F23.wireOp",EDGE,"E281"),sQuery(id+"F23.wireOp",EDGE,"E282"),sQuery(id+"F23.wireOp",EDGE,"E283"),sQuery(id+"F23.wireOp",EDGE,"E284"),sQuery(id+"F23.wireOp",EDGE,"E285"),sQuery(id+"F23.wireOp",EDGE,"E286"),sQuery(id+"F23.wireOp",EDGE,"E287"),sQuery(id+"F23.wireOp",EDGE,"E288")])],"isStart":true})]});
            var sketch = newSketch(context, id + "F25", { "sketchPlane" : qUnion([Q0])});
            skLineSegment(sketch, "E289.bottom", {"start": v(0, 6000) * mm, "end": v(10000, 6000) * mm});
            skLineSegment(sketch, "E289.top", {"start": v(0, 0) * mm, "end": v(10000, 0) * mm});
            skLineSegment(sketch, "E289.left", {"start": v(0, 6000) * mm, "end": v(0, 0) * mm});
            skLineSegment(sketch, "E289.right", {"start": v(10000, 6000) * mm, "end": v(10000, 0) * mm});
            skSolve(sketch);
        }
        {
            var Q0;
            Q0=qSketchRegion(id+"F25",true);
            extrude(context, id + "F26", {"entities" : qUnion([Q0]), "operationType" : NewBodyOperationType.ADD, "depth" : 25 * mm, "offsetDistance" : 25 * mm});
        }
        {
            var Q0;
            Q0=makeQuery(id+"F26.boolean.opBoolean","MERGE",FACE,{"derivedFrom":[makeQuery(id+"F22.boolean.opBoolean","MERGE",FACE,{"derivedFrom":[makeQuery(id+"F12.opExtrude","CAP_FACE",FACE,{"disambiguationData":[OSD([sQuery(id+"F0.wireOp",EDGE,"E0.top"),sQuery(id+"F1.wireOp",EDGE,"E1.top"),sQuery(id+"F5.wireOp",EDGE,"E53.top"),sQuery(id+"F7.wireOp",EDGE,"E54.top"),sQuery(id+"F7.wireOp",EDGE,"E116")])],"isStart":false}),makeQuery(id+"F22.opExtrude","SWEPT_FACE",FACE,{"disambiguationData":[OSD([sQuery(id+"F21.wireOp",EDGE,"E157.bottom")])]})]}),makeQuery(id+"F26.opExtrude","SWEPT_FACE",FACE,{"disambiguationData":[OSD([sQuery(id+"F25.wireOp",EDGE,"E289.bottom")])]})]});
            var sketch = newSketch(context, id + "F27", { "sketchPlane" : qUnion([Q0])});
            skLineSegment(sketch, "E290.bottom", {"start": v(-3850, 1500) * mm, "end": v(-2850, 1500) * mm});
            skLineSegment(sketch, "E290.top", {"start": v(-3850, 750) * mm, "end": v(-2850, 750) * mm});
            skLineSegment(sketch, "E290.left", {"start": v(-3850, 1500) * mm, "end": v(-3850, 750) * mm});
            skLineSegment(sketch, "E290.right", {"start": v(-2850, 1500) * mm, "end": v(-2850, 750) * mm});
            skLineSegment(sketch, "E291.bottom", {"start": v(-1750, 1500) * mm, "end": v(-750, 1500) * mm});
            skLineSegment(sketch, "E291.top", {"start": v(-1750, 750) * mm, "end": v(-750, 750) * mm});
            skLineSegment(sketch, "E291.left", {"start": v(-1750, 1500) * mm, "end": v(-1750, 750) * mm});
            skLineSegment(sketch, "E291.right", {"start": v(-750, 1500) * mm, "end": v(-750, 750) * mm});
            skLineSegment(sketch, "E292.bottom", {"start": v(-3850, 3792.4) * mm, "end": v(-2850, 3792.4) * mm});
            skLineSegment(sketch, "E292.top", {"start": v(-3850, 4542.4) * mm, "end": v(-2850, 4542.4) * mm});
            skLineSegment(sketch, "E292.left", {"start": v(-3850, 3792.4) * mm, "end": v(-3850, 4542.4) * mm});
            skLineSegment(sketch, "E292.right", {"start": v(-2850, 3792.4) * mm, "end": v(-2850, 4542.4) * mm});
            skLineSegment(sketch, "E293.bottom", {"start": v(-1750, 3792.4) * mm, "end": v(-750, 3792.4) * mm});
            skLineSegment(sketch, "E293.top", {"start": v(-1750, 4542.4) * mm, "end": v(-750, 4542.4) * mm});
            skLineSegment(sketch, "E293.left", {"start": v(-1750, 3792.4) * mm, "end": v(-1750, 4542.4) * mm});
            skLineSegment(sketch, "E293.right", {"start": v(-750, 3792.4) * mm, "end": v(-750, 4542.4) * mm});
            skLineSegment(sketch, "E294.bottom", {"start": v(-9250, 1500) * mm, "end": v(-8250, 1500) * mm});
            skLineSegment(sketch, "E294.top", {"start": v(-9250, 750) * mm, "end": v(-8250, 750) * mm});
            skLineSegment(sketch, "E294.left", {"start": v(-9250, 1500) * mm, "end": v(-9250, 750) * mm});
            skLineSegment(sketch, "E294.right", {"start": v(-8250, 1500) * mm, "end": v(-8250, 750) * mm});
            skLineSegment(sketch, "E295.bottom", {"start": v(-7150, 1500) * mm, "end": v(-6150, 1500) * mm});
            skLineSegment(sketch, "E295.top", {"start": v(-7150, 750) * mm, "end": v(-6150, 750) * mm});
            skLineSegment(sketch, "E295.left", {"start": v(-7150, 1500) * mm, "end": v(-7150, 750) * mm});
            skLineSegment(sketch, "E295.right", {"start": v(-6150, 1500) * mm, "end": v(-6150, 750) * mm});
            skLineSegment(sketch, "E296.bottom", {"start": v(-9250, 3792.4) * mm, "end": v(-8250, 3792.4) * mm});
            skLineSegment(sketch, "E296.top", {"start": v(-9250, 4542.4) * mm, "end": v(-8250, 4542.4) * mm});
            skLineSegment(sketch, "E296.left", {"start": v(-9250, 3792.4) * mm, "end": v(-9250, 4542.4) * mm});
            skLineSegment(sketch, "E296.right", {"start": v(-8250, 3792.4) * mm, "end": v(-8250, 4542.4) * mm});
            skLineSegment(sketch, "E297.bottom", {"start": v(-7150, 3792.4) * mm, "end": v(-6150, 3792.4) * mm});
            skLineSegment(sketch, "E297.top", {"start": v(-7150, 4542.4) * mm, "end": v(-6150, 4542.4) * mm});
            skLineSegment(sketch, "E297.left", {"start": v(-7150, 3792.4) * mm, "end": v(-7150, 4542.4) * mm});
            skLineSegment(sketch, "E297.right", {"start": v(-6150, 3792.4) * mm, "end": v(-6150, 4542.4) * mm});
            skSolve(sketch);
        }
        {
            var Q0;
            Q0=qSketchRegion(id+"F27",true);
            extrude(context, id + "F28", {"entities" : qUnion([Q0]), "operationType" : NewBodyOperationType.REMOVE, "oppositeDirection" : true, "depth" : 50 * mm, "offsetDistance" : 25 * mm});
        }
        {
            var Q0;
            {var subQ0=makeQuery(id+"F6.boolean.opBoolean","MERGE",FACE,{"derivedFrom":[makeQuery(id+"F3.boolean.opBoolean","MERGE",FACE,{"derivedFrom":[makeQuery(id+"F2.opExtrude","SWEPT_FACE",FACE,{"disambiguationData":[OSD([sQuery(id+"F0.wireOp",EDGE,"E0.bottom")])]}),makeQuery(id+"F3.opExtrude","SWEPT_FACE",FACE,{"disambiguationData":[OSD([sQuery(id+"F1.wireOp",EDGE,"E1.bottom")])]})]}),makeQuery(id+"F6.opExtrude","SWEPT_FACE",FACE,{"disambiguationData":[OSD([sQuery(id+"F5.wireOp",EDGE,"E53.bottom")])]})]});Q0=makeQuery(id+"F26.boolean.opBoolean","MERGE",FACE,{"derivedFrom":[makeQuery(id+"F22.boolean.opBoolean","MERGE",FACE,{"derivedFrom":[makeQuery(id+"F9.boolean.opBoolean","MERGE",FACE,{"derivedFrom":[subQ0,makeQuery(id+"F9.opPattern","COPY",FACE,{"derivedFrom":subQ0,"instanceName":"1"})]}),makeQuery(id+"F22.opExtrude","SWEPT_FACE",FACE,{"disambiguationData":[OSD([sQuery(id+"F21.wireOp",EDGE,"E157.top")])]})]}),makeQuery(id+"F26.opExtrude","SWEPT_FACE",FACE,{"disambiguationData":[OSD([sQuery(id+"F25.wireOp",EDGE,"E289.top")])]})]});}
            var sketch = newSketch(context, id + "F29", { "sketchPlane" : qUnion([Q0])});
            skLineSegment(sketch, "E298.bottom", {"start": v(6150, 1475) * mm, "end": v(7150, 1475) * mm});
            skLineSegment(sketch, "E298.top", {"start": v(6150, 725) * mm, "end": v(7150, 725) * mm});
            skLineSegment(sketch, "E298.left", {"start": v(6150, 1475) * mm, "end": v(6150, 725) * mm});
            skLineSegment(sketch, "E298.right", {"start": v(7150, 1475) * mm, "end": v(7150, 725) * mm});
            skLineSegment(sketch, "E299.bottom", {"start": v(8250, 1475) * mm, "end": v(9250, 1475) * mm});
            skLineSegment(sketch, "E299.top", {"start": v(8250, 725) * mm, "end": v(9250, 725) * mm});
            skLineSegment(sketch, "E299.left", {"start": v(8250, 1475) * mm, "end": v(8250, 725) * mm});
            skLineSegment(sketch, "E299.right", {"start": v(9250, 1475) * mm, "end": v(9250, 725) * mm});
            skLineSegment(sketch, "E300.bottom", {"start": v(6150, 3762.4) * mm, "end": v(7150, 3762.4) * mm});
            skLineSegment(sketch, "E300.top", {"start": v(6150, 4512.4) * mm, "end": v(7150, 4512.4) * mm});
            skLineSegment(sketch, "E300.left", {"start": v(6150, 3762.4) * mm, "end": v(6150, 4512.4) * mm});
            skLineSegment(sketch, "E300.right", {"start": v(7150, 3762.4) * mm, "end": v(7150, 4512.4) * mm});
            skLineSegment(sketch, "E301.bottom", {"start": v(8250, 3762.4) * mm, "end": v(9250, 3762.4) * mm});
            skLineSegment(sketch, "E301.top", {"start": v(8250, 4512.4) * mm, "end": v(9250, 4512.4) * mm});
            skLineSegment(sketch, "E301.left", {"start": v(8250, 3762.4) * mm, "end": v(8250, 4512.4) * mm});
            skLineSegment(sketch, "E301.right", {"start": v(9250, 3762.4) * mm, "end": v(9250, 4512.4) * mm});
            skLineSegment(sketch, "E302.bottom", {"start": v(750, 1470) * mm, "end": v(1750, 1470) * mm});
            skLineSegment(sketch, "E302.top", {"start": v(750, 720) * mm, "end": v(1750, 720) * mm});
            skLineSegment(sketch, "E302.left", {"start": v(750, 1470) * mm, "end": v(750, 720) * mm});
            skLineSegment(sketch, "E302.right", {"start": v(1750, 1470) * mm, "end": v(1750, 720) * mm});
            skLineSegment(sketch, "E303.bottom", {"start": v(2850, 1470) * mm, "end": v(3850, 1470) * mm});
            skLineSegment(sketch, "E303.top", {"start": v(2850, 720) * mm, "end": v(3850, 720) * mm});
            skLineSegment(sketch, "E303.left", {"start": v(2850, 1470) * mm, "end": v(2850, 720) * mm});
            skLineSegment(sketch, "E303.right", {"start": v(3850, 1470) * mm, "end": v(3850, 720) * mm});
            skLineSegment(sketch, "E304.bottom", {"start": v(750, 3762.4) * mm, "end": v(1750, 3762.4) * mm});
            skLineSegment(sketch, "E304.top", {"start": v(750, 4512.4) * mm, "end": v(1750, 4512.4) * mm});
            skLineSegment(sketch, "E304.left", {"start": v(750, 3762.4) * mm, "end": v(750, 4512.4) * mm});
            skLineSegment(sketch, "E304.right", {"start": v(1750, 3762.4) * mm, "end": v(1750, 4512.4) * mm});
            skLineSegment(sketch, "E305.bottom", {"start": v(2850, 3762.4) * mm, "end": v(3850, 3762.4) * mm});
            skLineSegment(sketch, "E305.top", {"start": v(2850, 4512.4) * mm, "end": v(3850, 4512.4) * mm});
            skLineSegment(sketch, "E305.left", {"start": v(2850, 3762.4) * mm, "end": v(2850, 4512.4) * mm});
            skLineSegment(sketch, "E305.right", {"start": v(3850, 3762.4) * mm, "end": v(3850, 4512.4) * mm});
            skSolve(sketch);
        }
        {
            var Q0;
            Q0=qSketchRegion(id+"F29",true);
            extrude(context, id + "F30", {"entities" : qUnion([Q0]), "operationType" : NewBodyOperationType.REMOVE, "oppositeDirection" : true, "depth" : 50 * mm, "offsetDistance" : 25 * mm});
        }
        {
            var Q0;
            Q0=makeQuery(id+"F26.boolean.opBoolean","MERGE",FACE,{"derivedFrom":[makeQuery(id+"F22.boolean.opBoolean","MERGE",FACE,{"derivedFrom":[makeQuery(id+"F9.boolean.opBoolean","MERGE",FACE,{"derivedFrom":[makeQuery(id+"F2.opExtrude","SWEPT_FACE",FACE,{"disambiguationData":[OSD([sQuery(id+"F0.wireOp",EDGE,"E0.right")])]}),makeQuery(id+"F6.opExtrude","SWEPT_FACE",FACE,{"disambiguationData":[OSD([sQuery(id+"F5.wireOp",EDGE,"E53.right")])]}),makeQuery(id+"F9.opPattern","COPY",FACE,{"derivedFrom":makeQuery(id+"F8.boolean.opBoolean","MERGE",FACE,{"derivedFrom":[makeQuery(id+"F6.boolean.opBoolean","MERGE",FACE,{"derivedFrom":[makeQuery(id+"F3.boolean.opBoolean","MERGE",FACE,{"derivedFrom":[makeQuery(id+"F2.opExtrude","SWEPT_FACE",FACE,{"disambiguationData":[OSD([sQuery(id+"F0.wireOp",EDGE,"E0.left")])]}),makeQuery(id+"F3.opExtrude","SWEPT_FACE",FACE,{"disambiguationData":[OSD([sQuery(id+"F1.wireOp",EDGE,"E1.left")])]}),makeQuery(id+"F3.opExtrude","SWEPT_FACE",FACE,{"disambiguationData":[OSD([sQuery(id+"F1.wireOp",EDGE,"E22.trimOffspring")])]})]}),makeQuery(id+"F6.opExtrude","SWEPT_FACE",FACE,{"disambiguationData":[OSD([sQuery(id+"F5.wireOp",EDGE,"E53.left")])]})]}),makeQuery(id+"F8.opExtrude","SWEPT_FACE",FACE,{"disambiguationData":[OSD([sQuery(id+"F7.wireOp",EDGE,"E54.left"),sQuery(id+"F7.wireOp",EDGE,"E75.trimOffspring"),sQuery(id+"F7.wireOp",EDGE,"E106")])]})]}),"instanceName":"1"})]}),makeQuery(id+"F22.opExtrude","SWEPT_FACE",FACE,{"disambiguationData":[OSD([sQuery(id+"F21.wireOp",EDGE,"E157.right")])]})]}),makeQuery(id+"F26.opExtrude","SWEPT_FACE",FACE,{"disambiguationData":[OSD([sQuery(id+"F25.wireOp",EDGE,"E289.right")])]})]});
            var sketch = newSketch(context, id + "F31", { "sketchPlane" : qUnion([Q0])});
            skLineSegment(sketch, "E306.bottom", {"start": v(600, 1475) * mm, "end": v(1600, 1475) * mm});
            skLineSegment(sketch, "E306.top", {"start": v(600, 725) * mm, "end": v(1600, 725) * mm});
            skLineSegment(sketch, "E306.left", {"start": v(600, 1475) * mm, "end": v(600, 725) * mm});
            skLineSegment(sketch, "E306.right", {"start": v(1600, 1475) * mm, "end": v(1600, 725) * mm});
            skLineSegment(sketch, "E307.bottom", {"start": v(4000, 1475) * mm, "end": v(5000, 1475) * mm});
            skLineSegment(sketch, "E307.top", {"start": v(4000, 725) * mm, "end": v(5000, 725) * mm});
            skLineSegment(sketch, "E307.left", {"start": v(4000, 1475) * mm, "end": v(4000, 725) * mm});
            skLineSegment(sketch, "E307.right", {"start": v(5000, 1475) * mm, "end": v(5000, 725) * mm});
            skLineSegment(sketch, "E308.bottom", {"start": v(600, 3775) * mm, "end": v(1600, 3775) * mm});
            skLineSegment(sketch, "E308.top", {"start": v(600, 4525) * mm, "end": v(1600, 4525) * mm});
            skLineSegment(sketch, "E308.left", {"start": v(600, 3775) * mm, "end": v(600, 4525) * mm});
            skLineSegment(sketch, "E308.right", {"start": v(1600, 3775) * mm, "end": v(1600, 4525) * mm});
            skLineSegment(sketch, "E309.bottom", {"start": v(4000, 3775) * mm, "end": v(5000, 3775) * mm});
            skLineSegment(sketch, "E309.top", {"start": v(4000, 4525) * mm, "end": v(5000, 4525) * mm});
            skLineSegment(sketch, "E309.left", {"start": v(4000, 3775) * mm, "end": v(4000, 4525) * mm});
            skLineSegment(sketch, "E309.right", {"start": v(5000, 3775) * mm, "end": v(5000, 4525) * mm});
            skSolve(sketch);
        }
        {
            var Q0;
            Q0=qSketchRegion(id+"F31",true);
            extrude(context, id + "F32", {"entities" : qUnion([Q0]), "operationType" : NewBodyOperationType.REMOVE, "oppositeDirection" : true, "depth" : 50 * mm, "offsetDistance" : 25 * mm});
        }
        {
            var Q0;
            {var subQ0=sQuery(id+"F7.wireOp",EDGE,"E109");var subQ1=sQuery(id+"F7.wireOp",EDGE,"E72.trimOffspring");var subQ2=sQuery(id+"F7.wireOp",EDGE,"E61");var subQ3=sQuery(id+"F7.wireOp",EDGE,"E56");var subQ4=sQuery(id+"F7.wireOp",EDGE,"E106");var subQ5=sQuery(id+"F7.wireOp",EDGE,"E75.trimOffspring");var subQ6=sQuery(id+"F7.wireOp",EDGE,"E54.left");var subQ7=sQuery(id+"F7.wireOp",EDGE,"E107");var subQ8=sQuery(id+"F7.wireOp",EDGE,"E112");var subQ9=sQuery(id+"F7.wireOp",EDGE,"E110");var subQ10=sQuery(id+"F7.wireOp",EDGE,"E73.trimOffspring");var subQ11=sQuery(id+"F7.wireOp",EDGE,"E71.trimOffspring");var subQ12=sQuery(id+"F7.wireOp",EDGE,"E59");var subQ13=sQuery(id+"F7.wireOp",EDGE,"E55");Q0=makeQuery(id+"F9.opPattern","COPY",FACE,{"derivedFrom":makeQuery(id+"F8.boolean.opBoolean","SPLIT",FACE,{"disambiguationData":[TD([makeQuery(id+"F2.opExtrude","SWEPT_FACE",FACE,{"disambiguationData":[OSD([sQuery(id+"F0.wireOp",EDGE,"E0.left")])]})])],"derivedFrom":makeQuery(id+"F8.opExtrude","CAP_FACE",FACE,{"disambiguationData":[OSD([sQuery(id+"F7.wireOp",EDGE,"E54.bottom"),sQuery(id+"F7.wireOp",EDGE,"E54.top"),subQ6,subQ13,subQ3,subQ12,sQuery(id+"F7.wireOp",EDGE,"E60"),subQ2,sQuery(id+"F7.wireOp",EDGE,"E62"),subQ11,subQ1,subQ10,sQuery(id+"F7.wireOp",EDGE,"E74.trimOffspring"),subQ5,sQuery(id+"F7.wireOp",EDGE,"E77"),sQuery(id+"F7.wireOp",EDGE,"E78"),sQuery(id+"F7.wireOp",EDGE,"E79"),sQuery(id+"F7.wireOp",EDGE,"E81"),sQuery(id+"F7.wireOp",EDGE,"E82"),sQuery(id+"F7.wireOp",EDGE,"E84"),sQuery(id+"F7.wireOp",EDGE,"E85"),sQuery(id+"F7.wireOp",EDGE,"E86"),sQuery(id+"F7.wireOp",EDGE,"E87"),sQuery(id+"F7.wireOp",EDGE,"E89"),sQuery(id+"F7.wireOp",EDGE,"E90"),sQuery(id+"F7.wireOp",EDGE,"E91"),sQuery(id+"F7.wireOp",EDGE,"E93"),sQuery(id+"F7.wireOp",EDGE,"E94"),sQuery(id+"F7.wireOp",EDGE,"E95"),sQuery(id+"F7.wireOp",EDGE,"E96"),sQuery(id+"F7.wireOp",EDGE,"E97"),sQuery(id+"F7.wireOp",EDGE,"E100"),sQuery(id+"F7.wireOp",EDGE,"E101"),sQuery(id+"F7.wireOp",EDGE,"E102"),sQuery(id+"F7.wireOp",EDGE,"E103"),sQuery(id+"F7.wireOp",EDGE,"E104"),subQ4,subQ7,sQuery(id+"F7.wireOp",EDGE,"E108"),subQ0,subQ9,sQuery(id+"F7.wireOp",EDGE,"E111"),subQ8,sQuery(id+"F7.wireOp",EDGE,"E113"),sQuery(id+"F7.wireOp",EDGE,"E114"),sQuery(id+"F7.wireOp",EDGE,"E115"),sQuery(id+"F7.wireOp",EDGE,"E116"),sQuery(id+"F7.wireOp",EDGE,"E117"),sQuery(id+"F7.wireOp",EDGE,"E118")])],"isStart":false})}),"instanceName":"1"});}
            extrude(context, id + "F33", {"entities" : qUnion([Q0]), "depth" : 1750 * mm, "offsetDistance" : 25 * mm});
        }
        {
            var Q0;
            {var subQ0=sQuery(id+"F7.wireOp",EDGE,"E118");var subQ1=sQuery(id+"F7.wireOp",EDGE,"E116");var subQ2=sQuery(id+"F7.wireOp",EDGE,"E54.top");var subQ3=sQuery(id+"F7.wireOp",EDGE,"E117");var subQ4=makeQuery(id+"F8.boolean.opBoolean","SPLIT",FACE,{"disambiguationData":[TD([makeQuery(id+"F2.opExtrude","SWEPT_FACE",FACE,{"disambiguationData":[OSD([sQuery(id+"F0.wireOp",EDGE,"E0.top")])]})])],"derivedFrom":makeQuery(id+"F8.opExtrude","CAP_FACE",FACE,{"disambiguationData":[OSD([sQuery(id+"F7.wireOp",EDGE,"E54.bottom"),subQ2,sQuery(id+"F7.wireOp",EDGE,"E54.left"),sQuery(id+"F7.wireOp",EDGE,"E55"),sQuery(id+"F7.wireOp",EDGE,"E56"),sQuery(id+"F7.wireOp",EDGE,"E59"),sQuery(id+"F7.wireOp",EDGE,"E60"),sQuery(id+"F7.wireOp",EDGE,"E61"),sQuery(id+"F7.wireOp",EDGE,"E62"),sQuery(id+"F7.wireOp",EDGE,"E71.trimOffspring"),sQuery(id+"F7.wireOp",EDGE,"E72.trimOffspring"),sQuery(id+"F7.wireOp",EDGE,"E73.trimOffspring"),sQuery(id+"F7.wireOp",EDGE,"E74.trimOffspring"),sQuery(id+"F7.wireOp",EDGE,"E75.trimOffspring"),sQuery(id+"F7.wireOp",EDGE,"E77"),sQuery(id+"F7.wireOp",EDGE,"E78"),sQuery(id+"F7.wireOp",EDGE,"E79"),sQuery(id+"F7.wireOp",EDGE,"E81"),sQuery(id+"F7.wireOp",EDGE,"E82"),sQuery(id+"F7.wireOp",EDGE,"E84"),sQuery(id+"F7.wireOp",EDGE,"E85"),sQuery(id+"F7.wireOp",EDGE,"E86"),sQuery(id+"F7.wireOp",EDGE,"E87"),sQuery(id+"F7.wireOp",EDGE,"E89"),sQuery(id+"F7.wireOp",EDGE,"E90"),sQuery(id+"F7.wireOp",EDGE,"E91"),sQuery(id+"F7.wireOp",EDGE,"E93"),sQuery(id+"F7.wireOp",EDGE,"E94"),sQuery(id+"F7.wireOp",EDGE,"E95"),sQuery(id+"F7.wireOp",EDGE,"E96"),sQuery(id+"F7.wireOp",EDGE,"E97"),sQuery(id+"F7.wireOp",EDGE,"E100"),sQuery(id+"F7.wireOp",EDGE,"E101"),sQuery(id+"F7.wireOp",EDGE,"E102"),sQuery(id+"F7.wireOp",EDGE,"E103"),sQuery(id+"F7.wireOp",EDGE,"E104"),sQuery(id+"F7.wireOp",EDGE,"E106"),sQuery(id+"F7.wireOp",EDGE,"E107"),sQuery(id+"F7.wireOp",EDGE,"E108"),sQuery(id+"F7.wireOp",EDGE,"E109"),sQuery(id+"F7.wireOp",EDGE,"E110"),sQuery(id+"F7.wireOp",EDGE,"E111"),sQuery(id+"F7.wireOp",EDGE,"E112"),sQuery(id+"F7.wireOp",EDGE,"E113"),sQuery(id+"F7.wireOp",EDGE,"E114"),sQuery(id+"F7.wireOp",EDGE,"E115"),subQ1,subQ3,subQ0])],"isStart":false})});Q0=makeQuery(id+"F9.boolean.opBoolean","MERGE",FACE,{"derivedFrom":[subQ4,makeQuery(id+"F9.opPattern","COPY",FACE,{"derivedFrom":subQ4,"instanceName":"1"})]});}
            extrude(context, id + "F34", {"entities" : qUnion([Q0]), "depth" : 1750 * mm, "offsetDistance" : 25 * mm});
        }
    });
